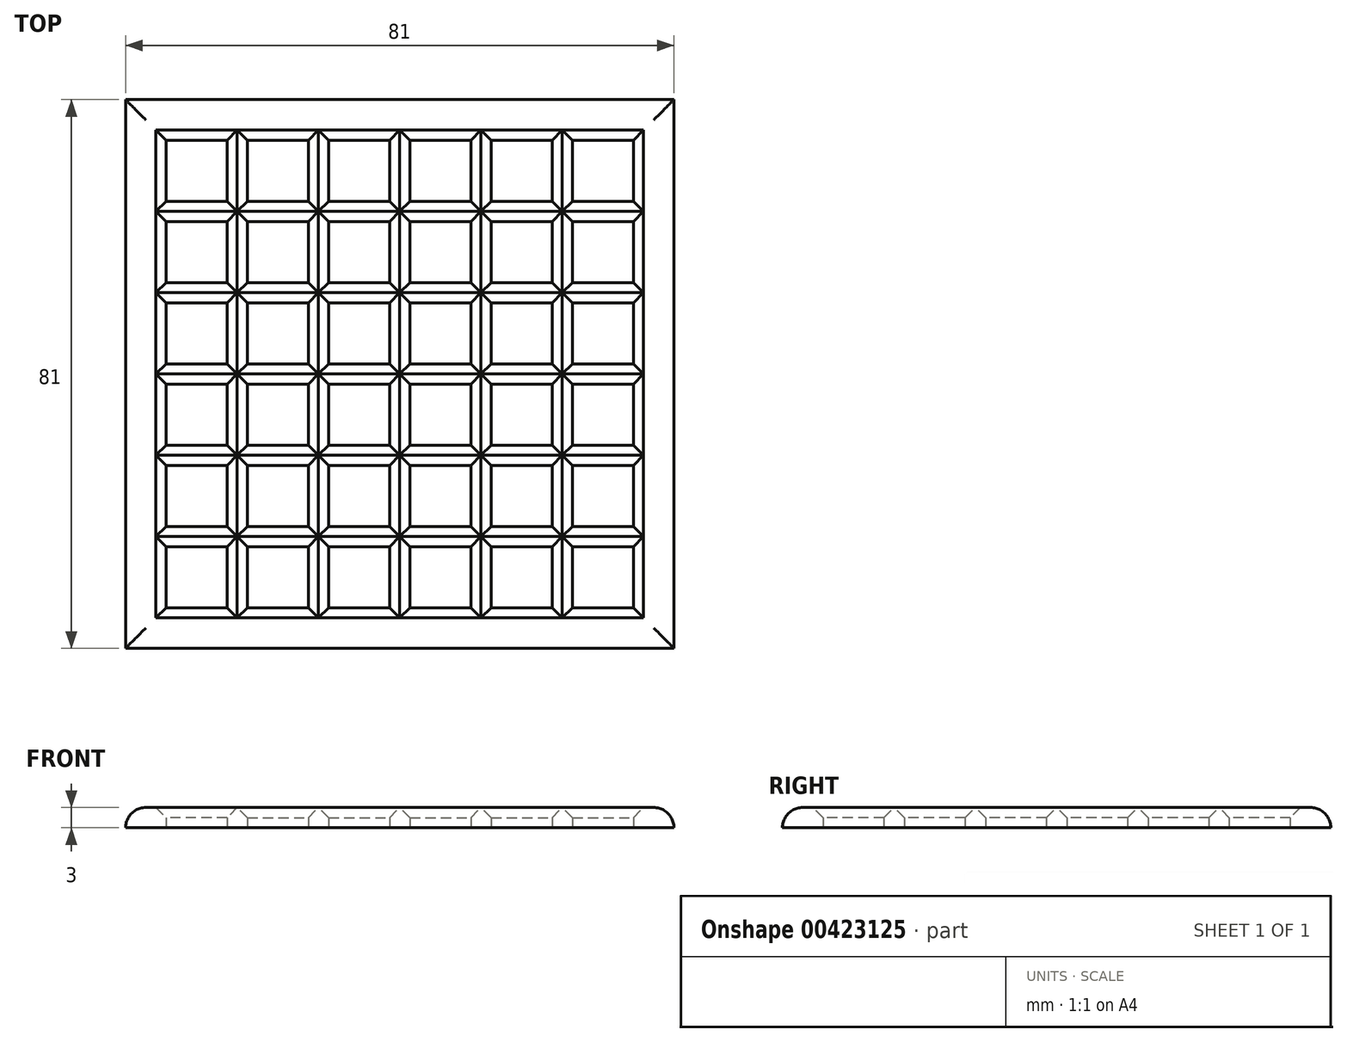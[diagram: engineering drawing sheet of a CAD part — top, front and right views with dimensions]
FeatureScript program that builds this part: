
annotation { "Feature Type Name" : "Feature", "Feature Type Description" : "" }
export const myFeature = defineFeature(function(context is Context, id is Id, definition is map)
    precondition{}
    {
        {
            var Q0;
            Q0=qCreatedBy(makeId("Top.planeOp"),FACE);
            var sketch = newSketch(context, id + "F0", { "sketchPlane" : qUnion([Q0])});
            skLineSegment(sketch, "E0.bottom", {"start": v(-69, 69) * mm, "end": v(-60, 69) * mm});
            skLineSegment(sketch, "E0.top", {"start": v(-69, 60) * mm, "end": v(-60, 60) * mm});
            skLineSegment(sketch, "E0.left", {"start": v(-69, 69) * mm, "end": v(-69, 60) * mm});
            skLineSegment(sketch, "E0.right", {"start": v(-60, 69) * mm, "end": v(-60, 60) * mm});
            skLineSegment(sketch, "E1.0.1.0", {"start": v(-69, 48) * mm, "end": v(-60, 48) * mm});
            skLineSegment(sketch, "E1.0.1.1", {"start": v(-60, 57) * mm, "end": v(-60, 48) * mm});
            skLineSegment(sketch, "E1.0.1.2", {"start": v(-69, 57) * mm, "end": v(-69, 48) * mm});
            skLineSegment(sketch, "E1.0.1.3", {"start": v(-69, 57) * mm, "end": v(-60, 57) * mm});
            skLineSegment(sketch, "E1.0.2.0", {"start": v(-69, 36) * mm, "end": v(-60, 36) * mm});
            skLineSegment(sketch, "E1.0.2.1", {"start": v(-60, 45) * mm, "end": v(-60, 36) * mm});
            skLineSegment(sketch, "E1.0.2.2", {"start": v(-69, 45) * mm, "end": v(-69, 36) * mm});
            skLineSegment(sketch, "E1.0.2.3", {"start": v(-69, 45) * mm, "end": v(-60, 45) * mm});
            skLineSegment(sketch, "E1.0.3.0", {"start": v(-69, 24) * mm, "end": v(-60, 24) * mm});
            skLineSegment(sketch, "E1.0.3.1", {"start": v(-60, 33) * mm, "end": v(-60, 24) * mm});
            skLineSegment(sketch, "E1.0.3.2", {"start": v(-69, 33) * mm, "end": v(-69, 24) * mm});
            skLineSegment(sketch, "E1.0.3.3", {"start": v(-69, 33) * mm, "end": v(-60, 33) * mm});
            skLineSegment(sketch, "E1.0.4.0", {"start": v(-69, 12) * mm, "end": v(-60, 12) * mm});
            skLineSegment(sketch, "E1.0.4.1", {"start": v(-60, 21) * mm, "end": v(-60, 12) * mm});
            skLineSegment(sketch, "E1.0.4.2", {"start": v(-69, 21) * mm, "end": v(-69, 12) * mm});
            skLineSegment(sketch, "E1.0.4.3", {"start": v(-69, 21) * mm, "end": v(-60, 21) * mm});
            skLineSegment(sketch, "E1.0.5.0", {"start": v(-69, 0) * mm, "end": v(-60, 0) * mm});
            skLineSegment(sketch, "E1.0.5.1", {"start": v(-60, 9) * mm, "end": v(-60, 0) * mm});
            skLineSegment(sketch, "E1.0.5.2", {"start": v(-69, 9) * mm, "end": v(-69, 0) * mm});
            skLineSegment(sketch, "E1.0.5.3", {"start": v(-69, 9) * mm, "end": v(-60, 9) * mm});
            skLineSegment(sketch, "E1.1.0.0", {"start": v(-57, 60) * mm, "end": v(-48, 60) * mm});
            skLineSegment(sketch, "E1.1.0.1", {"start": v(-48, 69) * mm, "end": v(-48, 60) * mm});
            skLineSegment(sketch, "E1.1.0.2", {"start": v(-57, 69) * mm, "end": v(-57, 60) * mm});
            skLineSegment(sketch, "E1.1.0.3", {"start": v(-57, 69) * mm, "end": v(-48, 69) * mm});
            skLineSegment(sketch, "E1.1.1.0", {"start": v(-57, 48) * mm, "end": v(-48, 48) * mm});
            skLineSegment(sketch, "E1.1.1.1", {"start": v(-48, 57) * mm, "end": v(-48, 48) * mm});
            skLineSegment(sketch, "E1.1.1.2", {"start": v(-57, 57) * mm, "end": v(-57, 48) * mm});
            skLineSegment(sketch, "E1.1.1.3", {"start": v(-57, 57) * mm, "end": v(-48, 57) * mm});
            skLineSegment(sketch, "E1.1.2.0", {"start": v(-57, 36) * mm, "end": v(-48, 36) * mm});
            skLineSegment(sketch, "E1.1.2.1", {"start": v(-48, 45) * mm, "end": v(-48, 36) * mm});
            skLineSegment(sketch, "E1.1.2.2", {"start": v(-57, 45) * mm, "end": v(-57, 36) * mm});
            skLineSegment(sketch, "E1.1.2.3", {"start": v(-57, 45) * mm, "end": v(-48, 45) * mm});
            skLineSegment(sketch, "E1.1.3.0", {"start": v(-57, 24) * mm, "end": v(-48, 24) * mm});
            skLineSegment(sketch, "E1.1.3.1", {"start": v(-48, 33) * mm, "end": v(-48, 24) * mm});
            skLineSegment(sketch, "E1.1.3.2", {"start": v(-57, 33) * mm, "end": v(-57, 24) * mm});
            skLineSegment(sketch, "E1.1.3.3", {"start": v(-57, 33) * mm, "end": v(-48, 33) * mm});
            skLineSegment(sketch, "E1.1.4.0", {"start": v(-57, 12) * mm, "end": v(-48, 12) * mm});
            skLineSegment(sketch, "E1.1.4.1", {"start": v(-48, 21) * mm, "end": v(-48, 12) * mm});
            skLineSegment(sketch, "E1.1.4.2", {"start": v(-57, 21) * mm, "end": v(-57, 12) * mm});
            skLineSegment(sketch, "E1.1.4.3", {"start": v(-57, 21) * mm, "end": v(-48, 21) * mm});
            skLineSegment(sketch, "E1.1.5.0", {"start": v(-57, 0) * mm, "end": v(-48, 0) * mm});
            skLineSegment(sketch, "E1.1.5.1", {"start": v(-48, 9) * mm, "end": v(-48, 0) * mm});
            skLineSegment(sketch, "E1.1.5.2", {"start": v(-57, 9) * mm, "end": v(-57, 0) * mm});
            skLineSegment(sketch, "E1.1.5.3", {"start": v(-57, 9) * mm, "end": v(-48, 9) * mm});
            skLineSegment(sketch, "E1.2.0.0", {"start": v(-45, 60) * mm, "end": v(-36, 60) * mm});
            skLineSegment(sketch, "E1.2.0.1", {"start": v(-36, 69) * mm, "end": v(-36, 60) * mm});
            skLineSegment(sketch, "E1.2.0.2", {"start": v(-45, 69) * mm, "end": v(-45, 60) * mm});
            skLineSegment(sketch, "E1.2.0.3", {"start": v(-45, 69) * mm, "end": v(-36, 69) * mm});
            skLineSegment(sketch, "E1.2.1.0", {"start": v(-45, 48) * mm, "end": v(-36, 48) * mm});
            skLineSegment(sketch, "E1.2.1.1", {"start": v(-36, 57) * mm, "end": v(-36, 48) * mm});
            skLineSegment(sketch, "E1.2.1.2", {"start": v(-45, 57) * mm, "end": v(-45, 48) * mm});
            skLineSegment(sketch, "E1.2.1.3", {"start": v(-45, 57) * mm, "end": v(-36, 57) * mm});
            skLineSegment(sketch, "E1.2.2.0", {"start": v(-45, 36) * mm, "end": v(-36, 36) * mm});
            skLineSegment(sketch, "E1.2.2.1", {"start": v(-36, 45) * mm, "end": v(-36, 36) * mm});
            skLineSegment(sketch, "E1.2.2.2", {"start": v(-45, 45) * mm, "end": v(-45, 36) * mm});
            skLineSegment(sketch, "E1.2.2.3", {"start": v(-45, 45) * mm, "end": v(-36, 45) * mm});
            skLineSegment(sketch, "E1.2.3.0", {"start": v(-45, 24) * mm, "end": v(-36, 24) * mm});
            skLineSegment(sketch, "E1.2.3.1", {"start": v(-36, 33) * mm, "end": v(-36, 24) * mm});
            skLineSegment(sketch, "E1.2.3.2", {"start": v(-45, 33) * mm, "end": v(-45, 24) * mm});
            skLineSegment(sketch, "E1.2.3.3", {"start": v(-45, 33) * mm, "end": v(-36, 33) * mm});
            skLineSegment(sketch, "E1.2.4.0", {"start": v(-45, 12) * mm, "end": v(-36, 12) * mm});
            skLineSegment(sketch, "E1.2.4.1", {"start": v(-36, 21) * mm, "end": v(-36, 12) * mm});
            skLineSegment(sketch, "E1.2.4.2", {"start": v(-45, 21) * mm, "end": v(-45, 12) * mm});
            skLineSegment(sketch, "E1.2.4.3", {"start": v(-45, 21) * mm, "end": v(-36, 21) * mm});
            skLineSegment(sketch, "E1.2.5.0", {"start": v(-45, 0) * mm, "end": v(-36, 0) * mm});
            skLineSegment(sketch, "E1.2.5.1", {"start": v(-36, 9) * mm, "end": v(-36, 0) * mm});
            skLineSegment(sketch, "E1.2.5.2", {"start": v(-45, 9) * mm, "end": v(-45, 0) * mm});
            skLineSegment(sketch, "E1.2.5.3", {"start": v(-45, 9) * mm, "end": v(-36, 9) * mm});
            skLineSegment(sketch, "E1.3.0.0", {"start": v(-33, 60) * mm, "end": v(-24, 60) * mm});
            skLineSegment(sketch, "E1.3.0.1", {"start": v(-24, 69) * mm, "end": v(-24, 60) * mm});
            skLineSegment(sketch, "E1.3.0.2", {"start": v(-33, 69) * mm, "end": v(-33, 60) * mm});
            skLineSegment(sketch, "E1.3.0.3", {"start": v(-33, 69) * mm, "end": v(-24, 69) * mm});
            skLineSegment(sketch, "E1.3.1.0", {"start": v(-33, 48) * mm, "end": v(-24, 48) * mm});
            skLineSegment(sketch, "E1.3.1.1", {"start": v(-24, 57) * mm, "end": v(-24, 48) * mm});
            skLineSegment(sketch, "E1.3.1.2", {"start": v(-33, 57) * mm, "end": v(-33, 48) * mm});
            skLineSegment(sketch, "E1.3.1.3", {"start": v(-33, 57) * mm, "end": v(-24, 57) * mm});
            skLineSegment(sketch, "E1.3.2.0", {"start": v(-33, 36) * mm, "end": v(-24, 36) * mm});
            skLineSegment(sketch, "E1.3.2.1", {"start": v(-24, 45) * mm, "end": v(-24, 36) * mm});
            skLineSegment(sketch, "E1.3.2.2", {"start": v(-33, 45) * mm, "end": v(-33, 36) * mm});
            skLineSegment(sketch, "E1.3.2.3", {"start": v(-33, 45) * mm, "end": v(-24, 45) * mm});
            skLineSegment(sketch, "E1.3.3.0", {"start": v(-33, 24) * mm, "end": v(-24, 24) * mm});
            skLineSegment(sketch, "E1.3.3.1", {"start": v(-24, 33) * mm, "end": v(-24, 24) * mm});
            skLineSegment(sketch, "E1.3.3.2", {"start": v(-33, 33) * mm, "end": v(-33, 24) * mm});
            skLineSegment(sketch, "E1.3.3.3", {"start": v(-33, 33) * mm, "end": v(-24, 33) * mm});
            skLineSegment(sketch, "E1.3.4.0", {"start": v(-33, 12) * mm, "end": v(-24, 12) * mm});
            skLineSegment(sketch, "E1.3.4.1", {"start": v(-24, 21) * mm, "end": v(-24, 12) * mm});
            skLineSegment(sketch, "E1.3.4.2", {"start": v(-33, 21) * mm, "end": v(-33, 12) * mm});
            skLineSegment(sketch, "E1.3.4.3", {"start": v(-33, 21) * mm, "end": v(-24, 21) * mm});
            skLineSegment(sketch, "E1.3.5.0", {"start": v(-33, 0) * mm, "end": v(-24, 0) * mm});
            skLineSegment(sketch, "E1.3.5.1", {"start": v(-24, 9) * mm, "end": v(-24, 0) * mm});
            skLineSegment(sketch, "E1.3.5.2", {"start": v(-33, 9) * mm, "end": v(-33, 0) * mm});
            skLineSegment(sketch, "E1.3.5.3", {"start": v(-33, 9) * mm, "end": v(-24, 9) * mm});
            skLineSegment(sketch, "E1.4.0.0", {"start": v(-21, 60) * mm, "end": v(-12, 60) * mm});
            skLineSegment(sketch, "E1.4.0.1", {"start": v(-12, 69) * mm, "end": v(-12, 60) * mm});
            skLineSegment(sketch, "E1.4.0.2", {"start": v(-21, 69) * mm, "end": v(-21, 60) * mm});
            skLineSegment(sketch, "E1.4.0.3", {"start": v(-21, 69) * mm, "end": v(-12, 69) * mm});
            skLineSegment(sketch, "E1.4.1.0", {"start": v(-21, 48) * mm, "end": v(-12, 48) * mm});
            skLineSegment(sketch, "E1.4.1.1", {"start": v(-12, 57) * mm, "end": v(-12, 48) * mm});
            skLineSegment(sketch, "E1.4.1.2", {"start": v(-21, 57) * mm, "end": v(-21, 48) * mm});
            skLineSegment(sketch, "E1.4.1.3", {"start": v(-21, 57) * mm, "end": v(-12, 57) * mm});
            skLineSegment(sketch, "E1.4.2.0", {"start": v(-21, 36) * mm, "end": v(-12, 36) * mm});
            skLineSegment(sketch, "E1.4.2.1", {"start": v(-12, 45) * mm, "end": v(-12, 36) * mm});
            skLineSegment(sketch, "E1.4.2.2", {"start": v(-21, 45) * mm, "end": v(-21, 36) * mm});
            skLineSegment(sketch, "E1.4.2.3", {"start": v(-21, 45) * mm, "end": v(-12, 45) * mm});
            skLineSegment(sketch, "E1.4.3.0", {"start": v(-21, 24) * mm, "end": v(-12, 24) * mm});
            skLineSegment(sketch, "E1.4.3.1", {"start": v(-12, 33) * mm, "end": v(-12, 24) * mm});
            skLineSegment(sketch, "E1.4.3.2", {"start": v(-21, 33) * mm, "end": v(-21, 24) * mm});
            skLineSegment(sketch, "E1.4.3.3", {"start": v(-21, 33) * mm, "end": v(-12, 33) * mm});
            skLineSegment(sketch, "E1.4.4.0", {"start": v(-21, 12) * mm, "end": v(-12, 12) * mm});
            skLineSegment(sketch, "E1.4.4.1", {"start": v(-12, 21) * mm, "end": v(-12, 12) * mm});
            skLineSegment(sketch, "E1.4.4.2", {"start": v(-21, 21) * mm, "end": v(-21, 12) * mm});
            skLineSegment(sketch, "E1.4.4.3", {"start": v(-21, 21) * mm, "end": v(-12, 21) * mm});
            skLineSegment(sketch, "E1.4.5.0", {"start": v(-21, 0) * mm, "end": v(-12, 0) * mm});
            skLineSegment(sketch, "E1.4.5.1", {"start": v(-12, 9) * mm, "end": v(-12, 0) * mm});
            skLineSegment(sketch, "E1.4.5.2", {"start": v(-21, 9) * mm, "end": v(-21, 0) * mm});
            skLineSegment(sketch, "E1.4.5.3", {"start": v(-21, 9) * mm, "end": v(-12, 9) * mm});
            skLineSegment(sketch, "E1.5.0.0", {"start": v(-9, 60) * mm, "end": v(0, 60) * mm});
            skLineSegment(sketch, "E1.5.0.1", {"start": v(0, 69) * mm, "end": v(0, 60) * mm});
            skLineSegment(sketch, "E1.5.0.2", {"start": v(-9, 69) * mm, "end": v(-9, 60) * mm});
            skLineSegment(sketch, "E1.5.0.3", {"start": v(-9, 69) * mm, "end": v(0, 69) * mm});
            skLineSegment(sketch, "E1.5.1.0", {"start": v(-9, 48) * mm, "end": v(0, 48) * mm});
            skLineSegment(sketch, "E1.5.1.1", {"start": v(0, 57) * mm, "end": v(0, 48) * mm});
            skLineSegment(sketch, "E1.5.1.2", {"start": v(-9, 57) * mm, "end": v(-9, 48) * mm});
            skLineSegment(sketch, "E1.5.1.3", {"start": v(-9, 57) * mm, "end": v(0, 57) * mm});
            skLineSegment(sketch, "E1.5.2.0", {"start": v(-9, 36) * mm, "end": v(0, 36) * mm});
            skLineSegment(sketch, "E1.5.2.1", {"start": v(0, 45) * mm, "end": v(0, 36) * mm});
            skLineSegment(sketch, "E1.5.2.2", {"start": v(-9, 45) * mm, "end": v(-9, 36) * mm});
            skLineSegment(sketch, "E1.5.2.3", {"start": v(-9, 45) * mm, "end": v(0, 45) * mm});
            skLineSegment(sketch, "E1.5.3.0", {"start": v(-9, 24) * mm, "end": v(0, 24) * mm});
            skLineSegment(sketch, "E1.5.3.1", {"start": v(0, 33) * mm, "end": v(0, 24) * mm});
            skLineSegment(sketch, "E1.5.3.2", {"start": v(-9, 33) * mm, "end": v(-9, 24) * mm});
            skLineSegment(sketch, "E1.5.3.3", {"start": v(-9, 33) * mm, "end": v(0, 33) * mm});
            skLineSegment(sketch, "E1.5.4.0", {"start": v(-9, 12) * mm, "end": v(0, 12) * mm});
            skLineSegment(sketch, "E1.5.4.1", {"start": v(0, 21) * mm, "end": v(0, 12) * mm});
            skLineSegment(sketch, "E1.5.4.2", {"start": v(-9, 21) * mm, "end": v(-9, 12) * mm});
            skLineSegment(sketch, "E1.5.4.3", {"start": v(-9, 21) * mm, "end": v(0, 21) * mm});
            skLineSegment(sketch, "E1.5.5.0", {"start": v(-9, 0) * mm, "end": v(0, 0) * mm});
            skLineSegment(sketch, "E1.5.5.1", {"start": v(0, 9) * mm, "end": v(0, 0) * mm});
            skLineSegment(sketch, "E1.5.5.2", {"start": v(-9, 9) * mm, "end": v(-9, 0) * mm});
            skLineSegment(sketch, "E1.5.5.3", {"start": v(-9, 9) * mm, "end": v(0, 9) * mm});
            skLineSegment(sketch, "E1.direction1", {"start": v(-69, 60) * mm, "end": v(-57, 60) * mm, "construction": true});
            skLineSegment(sketch, "E1.direction2", {"start": v(-69, 60) * mm, "end": v(-69, 48) * mm, "construction": true});
            skSolve(sketch);
        }
        {
            var Q0;
            Q0=qCreatedBy(makeId("Top.planeOp"),FACE);
            var sketch = newSketch(context, id + "F1", { "sketchPlane" : qUnion([Q0])});
            skLineSegment(sketch, "E2.bottom", {"start": v(-75, 75) * mm, "end": v(6, 75) * mm});
            skLineSegment(sketch, "E2.top", {"start": v(-75, -6) * mm, "end": v(6, -6) * mm});
            skLineSegment(sketch, "E2.left", {"start": v(-75, 75) * mm, "end": v(-75, -6) * mm});
            skLineSegment(sketch, "E2.right", {"start": v(6, 75) * mm, "end": v(6, -6) * mm});
            skSolve(sketch);
        }
        {
            var Q0;
            Q0=qSketchRegion(id+"F1",true);
            extrude(context, id + "F2", {"entities" : qUnion([Q0]), "depth" : 3 * mm});
        }
        {
            var Q0;
            Q0=qSketchRegion(id+"F0",true);
            extrude(context, id + "F3", {"entities" : qUnion([Q0]), "operationType" : NewBodyOperationType.REMOVE, "oppositeDirection" : true, "depth" : -5 * mm, "hasSecondDirection" : true, "secondDirectionOppositeDirection" : false, "secondDirectionDepth" : -3 * mm});
        }
        {
            var Q0;
            Q0=makeQuery(id+"F3.boolean.opBoolean","INTERSECT",EDGE,{"derivedFrom":[makeQuery(id+"F2.opExtrude","CAP_FACE",FACE,{"disambiguationData":[OSD([sQuery(id+"F1.wireOp",EDGE,"E2.bottom"),sQuery(id+"F1.wireOp",EDGE,"E2.top"),sQuery(id+"F1.wireOp",EDGE,"E2.left"),sQuery(id+"F1.wireOp",EDGE,"E2.right")])],"isStart":false}),makeQuery(id+"F3.opExtrude","SWEPT_FACE",FACE,{"disambiguationData":[OSD([sQuery(id+"F0.wireOp",EDGE,"E0.bottom")])]})]});
            var Q1;
            Q1=makeQuery(id+"F3.boolean.opBoolean","INTERSECT",EDGE,{"derivedFrom":[makeQuery(id+"F2.opExtrude","CAP_FACE",FACE,{"disambiguationData":[OSD([sQuery(id+"F1.wireOp",EDGE,"E2.bottom"),sQuery(id+"F1.wireOp",EDGE,"E2.top"),sQuery(id+"F1.wireOp",EDGE,"E2.left"),sQuery(id+"F1.wireOp",EDGE,"E2.right")])],"isStart":false}),makeQuery(id+"F3.opExtrude","SWEPT_FACE",FACE,{"disambiguationData":[OSD([sQuery(id+"F0.wireOp",EDGE,"E0.left")])]})]});
            var Q2;
            Q2=makeQuery(id+"F3.boolean.opBoolean","INTERSECT",EDGE,{"derivedFrom":[makeQuery(id+"F2.opExtrude","CAP_FACE",FACE,{"disambiguationData":[OSD([sQuery(id+"F1.wireOp",EDGE,"E2.bottom"),sQuery(id+"F1.wireOp",EDGE,"E2.top"),sQuery(id+"F1.wireOp",EDGE,"E2.left"),sQuery(id+"F1.wireOp",EDGE,"E2.right")])],"isStart":false}),makeQuery(id+"F3.opExtrude","SWEPT_FACE",FACE,{"disambiguationData":[OSD([sQuery(id+"F0.wireOp",EDGE,"E0.right")])]})]});
            var Q3;
            Q3=makeQuery(id+"F3.boolean.opBoolean","INTERSECT",EDGE,{"derivedFrom":[makeQuery(id+"F2.opExtrude","CAP_FACE",FACE,{"disambiguationData":[OSD([sQuery(id+"F1.wireOp",EDGE,"E2.bottom"),sQuery(id+"F1.wireOp",EDGE,"E2.top"),sQuery(id+"F1.wireOp",EDGE,"E2.left"),sQuery(id+"F1.wireOp",EDGE,"E2.right")])],"isStart":false}),makeQuery(id+"F3.opExtrude","SWEPT_FACE",FACE,{"disambiguationData":[OSD([sQuery(id+"F0.wireOp",EDGE,"E0.top")])]})]});
            var Q4;
            Q4=makeQuery(id+"F3.boolean.opBoolean","INTERSECT",EDGE,{"derivedFrom":[makeQuery(id+"F2.opExtrude","CAP_FACE",FACE,{"disambiguationData":[OSD([sQuery(id+"F1.wireOp",EDGE,"E2.bottom"),sQuery(id+"F1.wireOp",EDGE,"E2.top"),sQuery(id+"F1.wireOp",EDGE,"E2.left"),sQuery(id+"F1.wireOp",EDGE,"E2.right")])],"isStart":false}),makeQuery(id+"F3.opExtrude","SWEPT_FACE",FACE,{"disambiguationData":[OSD([sQuery(id+"F0.wireOp",EDGE,"E1.1.0.3")])]})]});
            var Q5;
            Q5=makeQuery(id+"F3.boolean.opBoolean","INTERSECT",EDGE,{"derivedFrom":[makeQuery(id+"F2.opExtrude","CAP_FACE",FACE,{"disambiguationData":[OSD([sQuery(id+"F1.wireOp",EDGE,"E2.bottom"),sQuery(id+"F1.wireOp",EDGE,"E2.top"),sQuery(id+"F1.wireOp",EDGE,"E2.left"),sQuery(id+"F1.wireOp",EDGE,"E2.right")])],"isStart":false}),makeQuery(id+"F3.opExtrude","SWEPT_FACE",FACE,{"disambiguationData":[OSD([sQuery(id+"F0.wireOp",EDGE,"E1.1.0.2")])]})]});
            var Q6;
            Q6=makeQuery(id+"F3.boolean.opBoolean","INTERSECT",EDGE,{"derivedFrom":[makeQuery(id+"F2.opExtrude","CAP_FACE",FACE,{"disambiguationData":[OSD([sQuery(id+"F1.wireOp",EDGE,"E2.bottom"),sQuery(id+"F1.wireOp",EDGE,"E2.top"),sQuery(id+"F1.wireOp",EDGE,"E2.left"),sQuery(id+"F1.wireOp",EDGE,"E2.right")])],"isStart":false}),makeQuery(id+"F3.opExtrude","SWEPT_FACE",FACE,{"disambiguationData":[OSD([sQuery(id+"F0.wireOp",EDGE,"E1.1.0.0")])]})]});
            var Q7;
            Q7=makeQuery(id+"F3.boolean.opBoolean","INTERSECT",EDGE,{"derivedFrom":[makeQuery(id+"F2.opExtrude","CAP_FACE",FACE,{"disambiguationData":[OSD([sQuery(id+"F1.wireOp",EDGE,"E2.bottom"),sQuery(id+"F1.wireOp",EDGE,"E2.top"),sQuery(id+"F1.wireOp",EDGE,"E2.left"),sQuery(id+"F1.wireOp",EDGE,"E2.right")])],"isStart":false}),makeQuery(id+"F3.opExtrude","SWEPT_FACE",FACE,{"disambiguationData":[OSD([sQuery(id+"F0.wireOp",EDGE,"E1.1.0.1")])]})]});
            var Q8;
            Q8=makeQuery(id+"F3.boolean.opBoolean","INTERSECT",EDGE,{"derivedFrom":[makeQuery(id+"F2.opExtrude","CAP_FACE",FACE,{"disambiguationData":[OSD([sQuery(id+"F1.wireOp",EDGE,"E2.bottom"),sQuery(id+"F1.wireOp",EDGE,"E2.top"),sQuery(id+"F1.wireOp",EDGE,"E2.left"),sQuery(id+"F1.wireOp",EDGE,"E2.right")])],"isStart":false}),makeQuery(id+"F3.opExtrude","SWEPT_FACE",FACE,{"disambiguationData":[OSD([sQuery(id+"F0.wireOp",EDGE,"E1.2.0.2")])]})]});
            var Q9;
            Q9=makeQuery(id+"F3.boolean.opBoolean","INTERSECT",EDGE,{"derivedFrom":[makeQuery(id+"F2.opExtrude","CAP_FACE",FACE,{"disambiguationData":[OSD([sQuery(id+"F1.wireOp",EDGE,"E2.bottom"),sQuery(id+"F1.wireOp",EDGE,"E2.top"),sQuery(id+"F1.wireOp",EDGE,"E2.left"),sQuery(id+"F1.wireOp",EDGE,"E2.right")])],"isStart":false}),makeQuery(id+"F3.opExtrude","SWEPT_FACE",FACE,{"disambiguationData":[OSD([sQuery(id+"F0.wireOp",EDGE,"E1.2.0.1")])]})]});
            var Q10;
            Q10=makeQuery(id+"F3.boolean.opBoolean","INTERSECT",EDGE,{"derivedFrom":[makeQuery(id+"F2.opExtrude","CAP_FACE",FACE,{"disambiguationData":[OSD([sQuery(id+"F1.wireOp",EDGE,"E2.bottom"),sQuery(id+"F1.wireOp",EDGE,"E2.top"),sQuery(id+"F1.wireOp",EDGE,"E2.left"),sQuery(id+"F1.wireOp",EDGE,"E2.right")])],"isStart":false}),makeQuery(id+"F3.opExtrude","SWEPT_FACE",FACE,{"disambiguationData":[OSD([sQuery(id+"F0.wireOp",EDGE,"E1.3.0.2")])]})]});
            var Q11;
            Q11=makeQuery(id+"F3.boolean.opBoolean","INTERSECT",EDGE,{"derivedFrom":[makeQuery(id+"F2.opExtrude","CAP_FACE",FACE,{"disambiguationData":[OSD([sQuery(id+"F1.wireOp",EDGE,"E2.bottom"),sQuery(id+"F1.wireOp",EDGE,"E2.top"),sQuery(id+"F1.wireOp",EDGE,"E2.left"),sQuery(id+"F1.wireOp",EDGE,"E2.right")])],"isStart":false}),makeQuery(id+"F3.opExtrude","SWEPT_FACE",FACE,{"disambiguationData":[OSD([sQuery(id+"F0.wireOp",EDGE,"E1.3.0.1")])]})]});
            var Q12;
            Q12=makeQuery(id+"F3.boolean.opBoolean","INTERSECT",EDGE,{"derivedFrom":[makeQuery(id+"F2.opExtrude","CAP_FACE",FACE,{"disambiguationData":[OSD([sQuery(id+"F1.wireOp",EDGE,"E2.bottom"),sQuery(id+"F1.wireOp",EDGE,"E2.top"),sQuery(id+"F1.wireOp",EDGE,"E2.left"),sQuery(id+"F1.wireOp",EDGE,"E2.right")])],"isStart":false}),makeQuery(id+"F3.opExtrude","SWEPT_FACE",FACE,{"disambiguationData":[OSD([sQuery(id+"F0.wireOp",EDGE,"E1.4.0.2")])]})]});
            var Q13;
            Q13=makeQuery(id+"F3.boolean.opBoolean","INTERSECT",EDGE,{"derivedFrom":[makeQuery(id+"F2.opExtrude","CAP_FACE",FACE,{"disambiguationData":[OSD([sQuery(id+"F1.wireOp",EDGE,"E2.bottom"),sQuery(id+"F1.wireOp",EDGE,"E2.top"),sQuery(id+"F1.wireOp",EDGE,"E2.left"),sQuery(id+"F1.wireOp",EDGE,"E2.right")])],"isStart":false}),makeQuery(id+"F3.opExtrude","SWEPT_FACE",FACE,{"disambiguationData":[OSD([sQuery(id+"F0.wireOp",EDGE,"E1.4.0.1")])]})]});
            var Q14;
            Q14=makeQuery(id+"F3.boolean.opBoolean","INTERSECT",EDGE,{"derivedFrom":[makeQuery(id+"F2.opExtrude","CAP_FACE",FACE,{"disambiguationData":[OSD([sQuery(id+"F1.wireOp",EDGE,"E2.bottom"),sQuery(id+"F1.wireOp",EDGE,"E2.top"),sQuery(id+"F1.wireOp",EDGE,"E2.left"),sQuery(id+"F1.wireOp",EDGE,"E2.right")])],"isStart":false}),makeQuery(id+"F3.opExtrude","SWEPT_FACE",FACE,{"disambiguationData":[OSD([sQuery(id+"F0.wireOp",EDGE,"E1.5.0.2")])]})]});
            var Q15;
            Q15=makeQuery(id+"F3.boolean.opBoolean","INTERSECT",EDGE,{"derivedFrom":[makeQuery(id+"F2.opExtrude","CAP_FACE",FACE,{"disambiguationData":[OSD([sQuery(id+"F1.wireOp",EDGE,"E2.bottom"),sQuery(id+"F1.wireOp",EDGE,"E2.top"),sQuery(id+"F1.wireOp",EDGE,"E2.left"),sQuery(id+"F1.wireOp",EDGE,"E2.right")])],"isStart":false}),makeQuery(id+"F3.opExtrude","SWEPT_FACE",FACE,{"disambiguationData":[OSD([sQuery(id+"F0.wireOp",EDGE,"E1.5.0.1")])]})]});
            var Q16;
            Q16=makeQuery(id+"F3.boolean.opBoolean","INTERSECT",EDGE,{"derivedFrom":[makeQuery(id+"F2.opExtrude","CAP_FACE",FACE,{"disambiguationData":[OSD([sQuery(id+"F1.wireOp",EDGE,"E2.bottom"),sQuery(id+"F1.wireOp",EDGE,"E2.top"),sQuery(id+"F1.wireOp",EDGE,"E2.left"),sQuery(id+"F1.wireOp",EDGE,"E2.right")])],"isStart":false}),makeQuery(id+"F3.opExtrude","SWEPT_FACE",FACE,{"disambiguationData":[OSD([sQuery(id+"F0.wireOp",EDGE,"E1.0.1.2")])]})]});
            var Q17;
            Q17=makeQuery(id+"F3.boolean.opBoolean","INTERSECT",EDGE,{"derivedFrom":[makeQuery(id+"F2.opExtrude","CAP_FACE",FACE,{"disambiguationData":[OSD([sQuery(id+"F1.wireOp",EDGE,"E2.bottom"),sQuery(id+"F1.wireOp",EDGE,"E2.top"),sQuery(id+"F1.wireOp",EDGE,"E2.left"),sQuery(id+"F1.wireOp",EDGE,"E2.right")])],"isStart":false}),makeQuery(id+"F3.opExtrude","SWEPT_FACE",FACE,{"disambiguationData":[OSD([sQuery(id+"F0.wireOp",EDGE,"E1.0.1.1")])]})]});
            var Q18;
            Q18=makeQuery(id+"F3.boolean.opBoolean","INTERSECT",EDGE,{"derivedFrom":[makeQuery(id+"F2.opExtrude","CAP_FACE",FACE,{"disambiguationData":[OSD([sQuery(id+"F1.wireOp",EDGE,"E2.bottom"),sQuery(id+"F1.wireOp",EDGE,"E2.top"),sQuery(id+"F1.wireOp",EDGE,"E2.left"),sQuery(id+"F1.wireOp",EDGE,"E2.right")])],"isStart":false}),makeQuery(id+"F3.opExtrude","SWEPT_FACE",FACE,{"disambiguationData":[OSD([sQuery(id+"F0.wireOp",EDGE,"E1.1.1.2")])]})]});
            var Q19;
            Q19=makeQuery(id+"F3.boolean.opBoolean","INTERSECT",EDGE,{"derivedFrom":[makeQuery(id+"F2.opExtrude","CAP_FACE",FACE,{"disambiguationData":[OSD([sQuery(id+"F1.wireOp",EDGE,"E2.bottom"),sQuery(id+"F1.wireOp",EDGE,"E2.top"),sQuery(id+"F1.wireOp",EDGE,"E2.left"),sQuery(id+"F1.wireOp",EDGE,"E2.right")])],"isStart":false}),makeQuery(id+"F3.opExtrude","SWEPT_FACE",FACE,{"disambiguationData":[OSD([sQuery(id+"F0.wireOp",EDGE,"E1.1.1.1")])]})]});
            var Q20;
            Q20=makeQuery(id+"F3.boolean.opBoolean","INTERSECT",EDGE,{"derivedFrom":[makeQuery(id+"F2.opExtrude","CAP_FACE",FACE,{"disambiguationData":[OSD([sQuery(id+"F1.wireOp",EDGE,"E2.bottom"),sQuery(id+"F1.wireOp",EDGE,"E2.top"),sQuery(id+"F1.wireOp",EDGE,"E2.left"),sQuery(id+"F1.wireOp",EDGE,"E2.right")])],"isStart":false}),makeQuery(id+"F3.opExtrude","SWEPT_FACE",FACE,{"disambiguationData":[OSD([sQuery(id+"F0.wireOp",EDGE,"E1.2.1.2")])]})]});
            var Q21;
            Q21=makeQuery(id+"F3.boolean.opBoolean","INTERSECT",EDGE,{"derivedFrom":[makeQuery(id+"F2.opExtrude","CAP_FACE",FACE,{"disambiguationData":[OSD([sQuery(id+"F1.wireOp",EDGE,"E2.bottom"),sQuery(id+"F1.wireOp",EDGE,"E2.top"),sQuery(id+"F1.wireOp",EDGE,"E2.left"),sQuery(id+"F1.wireOp",EDGE,"E2.right")])],"isStart":false}),makeQuery(id+"F3.opExtrude","SWEPT_FACE",FACE,{"disambiguationData":[OSD([sQuery(id+"F0.wireOp",EDGE,"E1.2.1.1")])]})]});
            var Q22;
            Q22=makeQuery(id+"F3.boolean.opBoolean","INTERSECT",EDGE,{"derivedFrom":[makeQuery(id+"F2.opExtrude","CAP_FACE",FACE,{"disambiguationData":[OSD([sQuery(id+"F1.wireOp",EDGE,"E2.bottom"),sQuery(id+"F1.wireOp",EDGE,"E2.top"),sQuery(id+"F1.wireOp",EDGE,"E2.left"),sQuery(id+"F1.wireOp",EDGE,"E2.right")])],"isStart":false}),makeQuery(id+"F3.opExtrude","SWEPT_FACE",FACE,{"disambiguationData":[OSD([sQuery(id+"F0.wireOp",EDGE,"E1.3.1.2")])]})]});
            var Q23;
            Q23=makeQuery(id+"F3.boolean.opBoolean","INTERSECT",EDGE,{"derivedFrom":[makeQuery(id+"F2.opExtrude","CAP_FACE",FACE,{"disambiguationData":[OSD([sQuery(id+"F1.wireOp",EDGE,"E2.bottom"),sQuery(id+"F1.wireOp",EDGE,"E2.top"),sQuery(id+"F1.wireOp",EDGE,"E2.left"),sQuery(id+"F1.wireOp",EDGE,"E2.right")])],"isStart":false}),makeQuery(id+"F3.opExtrude","SWEPT_FACE",FACE,{"disambiguationData":[OSD([sQuery(id+"F0.wireOp",EDGE,"E1.3.1.1")])]})]});
            var Q24;
            Q24=makeQuery(id+"F3.boolean.opBoolean","INTERSECT",EDGE,{"derivedFrom":[makeQuery(id+"F2.opExtrude","CAP_FACE",FACE,{"disambiguationData":[OSD([sQuery(id+"F1.wireOp",EDGE,"E2.bottom"),sQuery(id+"F1.wireOp",EDGE,"E2.top"),sQuery(id+"F1.wireOp",EDGE,"E2.left"),sQuery(id+"F1.wireOp",EDGE,"E2.right")])],"isStart":false}),makeQuery(id+"F3.opExtrude","SWEPT_FACE",FACE,{"disambiguationData":[OSD([sQuery(id+"F0.wireOp",EDGE,"E1.4.1.2")])]})]});
            var Q25;
            Q25=makeQuery(id+"F3.boolean.opBoolean","INTERSECT",EDGE,{"derivedFrom":[makeQuery(id+"F2.opExtrude","CAP_FACE",FACE,{"disambiguationData":[OSD([sQuery(id+"F1.wireOp",EDGE,"E2.bottom"),sQuery(id+"F1.wireOp",EDGE,"E2.top"),sQuery(id+"F1.wireOp",EDGE,"E2.left"),sQuery(id+"F1.wireOp",EDGE,"E2.right")])],"isStart":false}),makeQuery(id+"F3.opExtrude","SWEPT_FACE",FACE,{"disambiguationData":[OSD([sQuery(id+"F0.wireOp",EDGE,"E1.4.1.1")])]})]});
            var Q26;
            Q26=makeQuery(id+"F3.boolean.opBoolean","INTERSECT",EDGE,{"derivedFrom":[makeQuery(id+"F2.opExtrude","CAP_FACE",FACE,{"disambiguationData":[OSD([sQuery(id+"F1.wireOp",EDGE,"E2.bottom"),sQuery(id+"F1.wireOp",EDGE,"E2.top"),sQuery(id+"F1.wireOp",EDGE,"E2.left"),sQuery(id+"F1.wireOp",EDGE,"E2.right")])],"isStart":false}),makeQuery(id+"F3.opExtrude","SWEPT_FACE",FACE,{"disambiguationData":[OSD([sQuery(id+"F0.wireOp",EDGE,"E1.5.1.2")])]})]});
            var Q27;
            Q27=makeQuery(id+"F3.boolean.opBoolean","INTERSECT",EDGE,{"derivedFrom":[makeQuery(id+"F2.opExtrude","CAP_FACE",FACE,{"disambiguationData":[OSD([sQuery(id+"F1.wireOp",EDGE,"E2.bottom"),sQuery(id+"F1.wireOp",EDGE,"E2.top"),sQuery(id+"F1.wireOp",EDGE,"E2.left"),sQuery(id+"F1.wireOp",EDGE,"E2.right")])],"isStart":false}),makeQuery(id+"F3.opExtrude","SWEPT_FACE",FACE,{"disambiguationData":[OSD([sQuery(id+"F0.wireOp",EDGE,"E1.5.1.1")])]})]});
            var Q28;
            Q28=makeQuery(id+"F3.boolean.opBoolean","INTERSECT",EDGE,{"derivedFrom":[makeQuery(id+"F2.opExtrude","CAP_FACE",FACE,{"disambiguationData":[OSD([sQuery(id+"F1.wireOp",EDGE,"E2.bottom"),sQuery(id+"F1.wireOp",EDGE,"E2.top"),sQuery(id+"F1.wireOp",EDGE,"E2.left"),sQuery(id+"F1.wireOp",EDGE,"E2.right")])],"isStart":false}),makeQuery(id+"F3.opExtrude","SWEPT_FACE",FACE,{"disambiguationData":[OSD([sQuery(id+"F0.wireOp",EDGE,"E1.0.2.2")])]})]});
            var Q29;
            Q29=makeQuery(id+"F3.boolean.opBoolean","INTERSECT",EDGE,{"derivedFrom":[makeQuery(id+"F2.opExtrude","CAP_FACE",FACE,{"disambiguationData":[OSD([sQuery(id+"F1.wireOp",EDGE,"E2.bottom"),sQuery(id+"F1.wireOp",EDGE,"E2.top"),sQuery(id+"F1.wireOp",EDGE,"E2.left"),sQuery(id+"F1.wireOp",EDGE,"E2.right")])],"isStart":false}),makeQuery(id+"F3.opExtrude","SWEPT_FACE",FACE,{"disambiguationData":[OSD([sQuery(id+"F0.wireOp",EDGE,"E1.0.2.1")])]})]});
            var Q30;
            Q30=makeQuery(id+"F3.boolean.opBoolean","INTERSECT",EDGE,{"derivedFrom":[makeQuery(id+"F2.opExtrude","CAP_FACE",FACE,{"disambiguationData":[OSD([sQuery(id+"F1.wireOp",EDGE,"E2.bottom"),sQuery(id+"F1.wireOp",EDGE,"E2.top"),sQuery(id+"F1.wireOp",EDGE,"E2.left"),sQuery(id+"F1.wireOp",EDGE,"E2.right")])],"isStart":false}),makeQuery(id+"F3.opExtrude","SWEPT_FACE",FACE,{"disambiguationData":[OSD([sQuery(id+"F0.wireOp",EDGE,"E1.1.2.2")])]})]});
            var Q31;
            Q31=makeQuery(id+"F3.boolean.opBoolean","INTERSECT",EDGE,{"derivedFrom":[makeQuery(id+"F2.opExtrude","CAP_FACE",FACE,{"disambiguationData":[OSD([sQuery(id+"F1.wireOp",EDGE,"E2.bottom"),sQuery(id+"F1.wireOp",EDGE,"E2.top"),sQuery(id+"F1.wireOp",EDGE,"E2.left"),sQuery(id+"F1.wireOp",EDGE,"E2.right")])],"isStart":false}),makeQuery(id+"F3.opExtrude","SWEPT_FACE",FACE,{"disambiguationData":[OSD([sQuery(id+"F0.wireOp",EDGE,"E1.1.2.1")])]})]});
            var Q32;
            Q32=makeQuery(id+"F3.boolean.opBoolean","INTERSECT",EDGE,{"derivedFrom":[makeQuery(id+"F2.opExtrude","CAP_FACE",FACE,{"disambiguationData":[OSD([sQuery(id+"F1.wireOp",EDGE,"E2.bottom"),sQuery(id+"F1.wireOp",EDGE,"E2.top"),sQuery(id+"F1.wireOp",EDGE,"E2.left"),sQuery(id+"F1.wireOp",EDGE,"E2.right")])],"isStart":false}),makeQuery(id+"F3.opExtrude","SWEPT_FACE",FACE,{"disambiguationData":[OSD([sQuery(id+"F0.wireOp",EDGE,"E1.2.2.2")])]})]});
            var Q33;
            Q33=makeQuery(id+"F3.boolean.opBoolean","INTERSECT",EDGE,{"derivedFrom":[makeQuery(id+"F2.opExtrude","CAP_FACE",FACE,{"disambiguationData":[OSD([sQuery(id+"F1.wireOp",EDGE,"E2.bottom"),sQuery(id+"F1.wireOp",EDGE,"E2.top"),sQuery(id+"F1.wireOp",EDGE,"E2.left"),sQuery(id+"F1.wireOp",EDGE,"E2.right")])],"isStart":false}),makeQuery(id+"F3.opExtrude","SWEPT_FACE",FACE,{"disambiguationData":[OSD([sQuery(id+"F0.wireOp",EDGE,"E1.2.2.1")])]})]});
            var Q34;
            Q34=makeQuery(id+"F3.boolean.opBoolean","INTERSECT",EDGE,{"derivedFrom":[makeQuery(id+"F2.opExtrude","CAP_FACE",FACE,{"disambiguationData":[OSD([sQuery(id+"F1.wireOp",EDGE,"E2.bottom"),sQuery(id+"F1.wireOp",EDGE,"E2.top"),sQuery(id+"F1.wireOp",EDGE,"E2.left"),sQuery(id+"F1.wireOp",EDGE,"E2.right")])],"isStart":false}),makeQuery(id+"F3.opExtrude","SWEPT_FACE",FACE,{"disambiguationData":[OSD([sQuery(id+"F0.wireOp",EDGE,"E1.3.2.2")])]})]});
            var Q35;
            Q35=makeQuery(id+"F3.boolean.opBoolean","INTERSECT",EDGE,{"derivedFrom":[makeQuery(id+"F2.opExtrude","CAP_FACE",FACE,{"disambiguationData":[OSD([sQuery(id+"F1.wireOp",EDGE,"E2.bottom"),sQuery(id+"F1.wireOp",EDGE,"E2.top"),sQuery(id+"F1.wireOp",EDGE,"E2.left"),sQuery(id+"F1.wireOp",EDGE,"E2.right")])],"isStart":false}),makeQuery(id+"F3.opExtrude","SWEPT_FACE",FACE,{"disambiguationData":[OSD([sQuery(id+"F0.wireOp",EDGE,"E1.3.2.1")])]})]});
            var Q36;
            Q36=makeQuery(id+"F3.boolean.opBoolean","INTERSECT",EDGE,{"derivedFrom":[makeQuery(id+"F2.opExtrude","CAP_FACE",FACE,{"disambiguationData":[OSD([sQuery(id+"F1.wireOp",EDGE,"E2.bottom"),sQuery(id+"F1.wireOp",EDGE,"E2.top"),sQuery(id+"F1.wireOp",EDGE,"E2.left"),sQuery(id+"F1.wireOp",EDGE,"E2.right")])],"isStart":false}),makeQuery(id+"F3.opExtrude","SWEPT_FACE",FACE,{"disambiguationData":[OSD([sQuery(id+"F0.wireOp",EDGE,"E1.4.2.2")])]})]});
            var Q37;
            Q37=makeQuery(id+"F3.boolean.opBoolean","INTERSECT",EDGE,{"derivedFrom":[makeQuery(id+"F2.opExtrude","CAP_FACE",FACE,{"disambiguationData":[OSD([sQuery(id+"F1.wireOp",EDGE,"E2.bottom"),sQuery(id+"F1.wireOp",EDGE,"E2.top"),sQuery(id+"F1.wireOp",EDGE,"E2.left"),sQuery(id+"F1.wireOp",EDGE,"E2.right")])],"isStart":false}),makeQuery(id+"F3.opExtrude","SWEPT_FACE",FACE,{"disambiguationData":[OSD([sQuery(id+"F0.wireOp",EDGE,"E1.4.2.1")])]})]});
            var Q38;
            Q38=makeQuery(id+"F3.boolean.opBoolean","INTERSECT",EDGE,{"derivedFrom":[makeQuery(id+"F2.opExtrude","CAP_FACE",FACE,{"disambiguationData":[OSD([sQuery(id+"F1.wireOp",EDGE,"E2.bottom"),sQuery(id+"F1.wireOp",EDGE,"E2.top"),sQuery(id+"F1.wireOp",EDGE,"E2.left"),sQuery(id+"F1.wireOp",EDGE,"E2.right")])],"isStart":false}),makeQuery(id+"F3.opExtrude","SWEPT_FACE",FACE,{"disambiguationData":[OSD([sQuery(id+"F0.wireOp",EDGE,"E1.5.2.2")])]})]});
            var Q39;
            Q39=makeQuery(id+"F3.boolean.opBoolean","INTERSECT",EDGE,{"derivedFrom":[makeQuery(id+"F2.opExtrude","CAP_FACE",FACE,{"disambiguationData":[OSD([sQuery(id+"F1.wireOp",EDGE,"E2.bottom"),sQuery(id+"F1.wireOp",EDGE,"E2.top"),sQuery(id+"F1.wireOp",EDGE,"E2.left"),sQuery(id+"F1.wireOp",EDGE,"E2.right")])],"isStart":false}),makeQuery(id+"F3.opExtrude","SWEPT_FACE",FACE,{"disambiguationData":[OSD([sQuery(id+"F0.wireOp",EDGE,"E1.5.2.1")])]})]});
            var Q40;
            Q40=makeQuery(id+"F3.boolean.opBoolean","INTERSECT",EDGE,{"derivedFrom":[makeQuery(id+"F2.opExtrude","CAP_FACE",FACE,{"disambiguationData":[OSD([sQuery(id+"F1.wireOp",EDGE,"E2.bottom"),sQuery(id+"F1.wireOp",EDGE,"E2.top"),sQuery(id+"F1.wireOp",EDGE,"E2.left"),sQuery(id+"F1.wireOp",EDGE,"E2.right")])],"isStart":false}),makeQuery(id+"F3.opExtrude","SWEPT_FACE",FACE,{"disambiguationData":[OSD([sQuery(id+"F0.wireOp",EDGE,"E1.0.3.2")])]})]});
            var Q41;
            Q41=makeQuery(id+"F3.boolean.opBoolean","INTERSECT",EDGE,{"derivedFrom":[makeQuery(id+"F2.opExtrude","CAP_FACE",FACE,{"disambiguationData":[OSD([sQuery(id+"F1.wireOp",EDGE,"E2.bottom"),sQuery(id+"F1.wireOp",EDGE,"E2.top"),sQuery(id+"F1.wireOp",EDGE,"E2.left"),sQuery(id+"F1.wireOp",EDGE,"E2.right")])],"isStart":false}),makeQuery(id+"F3.opExtrude","SWEPT_FACE",FACE,{"disambiguationData":[OSD([sQuery(id+"F0.wireOp",EDGE,"E1.0.3.1")])]})]});
            var Q42;
            Q42=makeQuery(id+"F3.boolean.opBoolean","INTERSECT",EDGE,{"derivedFrom":[makeQuery(id+"F2.opExtrude","CAP_FACE",FACE,{"disambiguationData":[OSD([sQuery(id+"F1.wireOp",EDGE,"E2.bottom"),sQuery(id+"F1.wireOp",EDGE,"E2.top"),sQuery(id+"F1.wireOp",EDGE,"E2.left"),sQuery(id+"F1.wireOp",EDGE,"E2.right")])],"isStart":false}),makeQuery(id+"F3.opExtrude","SWEPT_FACE",FACE,{"disambiguationData":[OSD([sQuery(id+"F0.wireOp",EDGE,"E1.1.3.2")])]})]});
            var Q43;
            Q43=makeQuery(id+"F3.boolean.opBoolean","INTERSECT",EDGE,{"derivedFrom":[makeQuery(id+"F2.opExtrude","CAP_FACE",FACE,{"disambiguationData":[OSD([sQuery(id+"F1.wireOp",EDGE,"E2.bottom"),sQuery(id+"F1.wireOp",EDGE,"E2.top"),sQuery(id+"F1.wireOp",EDGE,"E2.left"),sQuery(id+"F1.wireOp",EDGE,"E2.right")])],"isStart":false}),makeQuery(id+"F3.opExtrude","SWEPT_FACE",FACE,{"disambiguationData":[OSD([sQuery(id+"F0.wireOp",EDGE,"E1.1.3.1")])]})]});
            var Q44;
            Q44=makeQuery(id+"F3.boolean.opBoolean","INTERSECT",EDGE,{"derivedFrom":[makeQuery(id+"F2.opExtrude","CAP_FACE",FACE,{"disambiguationData":[OSD([sQuery(id+"F1.wireOp",EDGE,"E2.bottom"),sQuery(id+"F1.wireOp",EDGE,"E2.top"),sQuery(id+"F1.wireOp",EDGE,"E2.left"),sQuery(id+"F1.wireOp",EDGE,"E2.right")])],"isStart":false}),makeQuery(id+"F3.opExtrude","SWEPT_FACE",FACE,{"disambiguationData":[OSD([sQuery(id+"F0.wireOp",EDGE,"E1.2.3.2")])]})]});
            var Q45;
            Q45=makeQuery(id+"F3.boolean.opBoolean","INTERSECT",EDGE,{"derivedFrom":[makeQuery(id+"F2.opExtrude","CAP_FACE",FACE,{"disambiguationData":[OSD([sQuery(id+"F1.wireOp",EDGE,"E2.bottom"),sQuery(id+"F1.wireOp",EDGE,"E2.top"),sQuery(id+"F1.wireOp",EDGE,"E2.left"),sQuery(id+"F1.wireOp",EDGE,"E2.right")])],"isStart":false}),makeQuery(id+"F3.opExtrude","SWEPT_FACE",FACE,{"disambiguationData":[OSD([sQuery(id+"F0.wireOp",EDGE,"E1.2.3.1")])]})]});
            var Q46;
            Q46=makeQuery(id+"F3.boolean.opBoolean","INTERSECT",EDGE,{"derivedFrom":[makeQuery(id+"F2.opExtrude","CAP_FACE",FACE,{"disambiguationData":[OSD([sQuery(id+"F1.wireOp",EDGE,"E2.bottom"),sQuery(id+"F1.wireOp",EDGE,"E2.top"),sQuery(id+"F1.wireOp",EDGE,"E2.left"),sQuery(id+"F1.wireOp",EDGE,"E2.right")])],"isStart":false}),makeQuery(id+"F3.opExtrude","SWEPT_FACE",FACE,{"disambiguationData":[OSD([sQuery(id+"F0.wireOp",EDGE,"E1.3.3.2")])]})]});
            var Q47;
            Q47=makeQuery(id+"F3.boolean.opBoolean","INTERSECT",EDGE,{"derivedFrom":[makeQuery(id+"F2.opExtrude","CAP_FACE",FACE,{"disambiguationData":[OSD([sQuery(id+"F1.wireOp",EDGE,"E2.bottom"),sQuery(id+"F1.wireOp",EDGE,"E2.top"),sQuery(id+"F1.wireOp",EDGE,"E2.left"),sQuery(id+"F1.wireOp",EDGE,"E2.right")])],"isStart":false}),makeQuery(id+"F3.opExtrude","SWEPT_FACE",FACE,{"disambiguationData":[OSD([sQuery(id+"F0.wireOp",EDGE,"E1.3.3.1")])]})]});
            var Q48;
            Q48=makeQuery(id+"F3.boolean.opBoolean","INTERSECT",EDGE,{"derivedFrom":[makeQuery(id+"F2.opExtrude","CAP_FACE",FACE,{"disambiguationData":[OSD([sQuery(id+"F1.wireOp",EDGE,"E2.bottom"),sQuery(id+"F1.wireOp",EDGE,"E2.top"),sQuery(id+"F1.wireOp",EDGE,"E2.left"),sQuery(id+"F1.wireOp",EDGE,"E2.right")])],"isStart":false}),makeQuery(id+"F3.opExtrude","SWEPT_FACE",FACE,{"disambiguationData":[OSD([sQuery(id+"F0.wireOp",EDGE,"E1.4.3.2")])]})]});
            var Q49;
            Q49=makeQuery(id+"F3.boolean.opBoolean","INTERSECT",EDGE,{"derivedFrom":[makeQuery(id+"F2.opExtrude","CAP_FACE",FACE,{"disambiguationData":[OSD([sQuery(id+"F1.wireOp",EDGE,"E2.bottom"),sQuery(id+"F1.wireOp",EDGE,"E2.top"),sQuery(id+"F1.wireOp",EDGE,"E2.left"),sQuery(id+"F1.wireOp",EDGE,"E2.right")])],"isStart":false}),makeQuery(id+"F3.opExtrude","SWEPT_FACE",FACE,{"disambiguationData":[OSD([sQuery(id+"F0.wireOp",EDGE,"E1.4.3.1")])]})]});
            var Q50;
            Q50=makeQuery(id+"F3.boolean.opBoolean","INTERSECT",EDGE,{"derivedFrom":[makeQuery(id+"F2.opExtrude","CAP_FACE",FACE,{"disambiguationData":[OSD([sQuery(id+"F1.wireOp",EDGE,"E2.bottom"),sQuery(id+"F1.wireOp",EDGE,"E2.top"),sQuery(id+"F1.wireOp",EDGE,"E2.left"),sQuery(id+"F1.wireOp",EDGE,"E2.right")])],"isStart":false}),makeQuery(id+"F3.opExtrude","SWEPT_FACE",FACE,{"disambiguationData":[OSD([sQuery(id+"F0.wireOp",EDGE,"E1.5.3.2")])]})]});
            var Q51;
            Q51=makeQuery(id+"F3.boolean.opBoolean","INTERSECT",EDGE,{"derivedFrom":[makeQuery(id+"F2.opExtrude","CAP_FACE",FACE,{"disambiguationData":[OSD([sQuery(id+"F1.wireOp",EDGE,"E2.bottom"),sQuery(id+"F1.wireOp",EDGE,"E2.top"),sQuery(id+"F1.wireOp",EDGE,"E2.left"),sQuery(id+"F1.wireOp",EDGE,"E2.right")])],"isStart":false}),makeQuery(id+"F3.opExtrude","SWEPT_FACE",FACE,{"disambiguationData":[OSD([sQuery(id+"F0.wireOp",EDGE,"E1.5.3.1")])]})]});
            var Q52;
            Q52=makeQuery(id+"F3.boolean.opBoolean","INTERSECT",EDGE,{"derivedFrom":[makeQuery(id+"F2.opExtrude","CAP_FACE",FACE,{"disambiguationData":[OSD([sQuery(id+"F1.wireOp",EDGE,"E2.bottom"),sQuery(id+"F1.wireOp",EDGE,"E2.top"),sQuery(id+"F1.wireOp",EDGE,"E2.left"),sQuery(id+"F1.wireOp",EDGE,"E2.right")])],"isStart":false}),makeQuery(id+"F3.opExtrude","SWEPT_FACE",FACE,{"disambiguationData":[OSD([sQuery(id+"F0.wireOp",EDGE,"E1.5.4.1")])]})]});
            var Q53;
            Q53=makeQuery(id+"F3.boolean.opBoolean","INTERSECT",EDGE,{"derivedFrom":[makeQuery(id+"F2.opExtrude","CAP_FACE",FACE,{"disambiguationData":[OSD([sQuery(id+"F1.wireOp",EDGE,"E2.bottom"),sQuery(id+"F1.wireOp",EDGE,"E2.top"),sQuery(id+"F1.wireOp",EDGE,"E2.left"),sQuery(id+"F1.wireOp",EDGE,"E2.right")])],"isStart":false}),makeQuery(id+"F3.opExtrude","SWEPT_FACE",FACE,{"disambiguationData":[OSD([sQuery(id+"F0.wireOp",EDGE,"E1.5.4.2")])]})]});
            var Q54;
            Q54=makeQuery(id+"F3.boolean.opBoolean","INTERSECT",EDGE,{"derivedFrom":[makeQuery(id+"F2.opExtrude","CAP_FACE",FACE,{"disambiguationData":[OSD([sQuery(id+"F1.wireOp",EDGE,"E2.bottom"),sQuery(id+"F1.wireOp",EDGE,"E2.top"),sQuery(id+"F1.wireOp",EDGE,"E2.left"),sQuery(id+"F1.wireOp",EDGE,"E2.right")])],"isStart":false}),makeQuery(id+"F3.opExtrude","SWEPT_FACE",FACE,{"disambiguationData":[OSD([sQuery(id+"F0.wireOp",EDGE,"E1.4.4.1")])]})]});
            var Q55;
            Q55=makeQuery(id+"F3.boolean.opBoolean","INTERSECT",EDGE,{"derivedFrom":[makeQuery(id+"F2.opExtrude","CAP_FACE",FACE,{"disambiguationData":[OSD([sQuery(id+"F1.wireOp",EDGE,"E2.bottom"),sQuery(id+"F1.wireOp",EDGE,"E2.top"),sQuery(id+"F1.wireOp",EDGE,"E2.left"),sQuery(id+"F1.wireOp",EDGE,"E2.right")])],"isStart":false}),makeQuery(id+"F3.opExtrude","SWEPT_FACE",FACE,{"disambiguationData":[OSD([sQuery(id+"F0.wireOp",EDGE,"E1.4.4.2")])]})]});
            var Q56;
            Q56=makeQuery(id+"F3.boolean.opBoolean","INTERSECT",EDGE,{"derivedFrom":[makeQuery(id+"F2.opExtrude","CAP_FACE",FACE,{"disambiguationData":[OSD([sQuery(id+"F1.wireOp",EDGE,"E2.bottom"),sQuery(id+"F1.wireOp",EDGE,"E2.top"),sQuery(id+"F1.wireOp",EDGE,"E2.left"),sQuery(id+"F1.wireOp",EDGE,"E2.right")])],"isStart":false}),makeQuery(id+"F3.opExtrude","SWEPT_FACE",FACE,{"disambiguationData":[OSD([sQuery(id+"F0.wireOp",EDGE,"E1.3.4.1")])]})]});
            var Q57;
            Q57=makeQuery(id+"F3.boolean.opBoolean","INTERSECT",EDGE,{"derivedFrom":[makeQuery(id+"F2.opExtrude","CAP_FACE",FACE,{"disambiguationData":[OSD([sQuery(id+"F1.wireOp",EDGE,"E2.bottom"),sQuery(id+"F1.wireOp",EDGE,"E2.top"),sQuery(id+"F1.wireOp",EDGE,"E2.left"),sQuery(id+"F1.wireOp",EDGE,"E2.right")])],"isStart":false}),makeQuery(id+"F3.opExtrude","SWEPT_FACE",FACE,{"disambiguationData":[OSD([sQuery(id+"F0.wireOp",EDGE,"E1.3.4.2")])]})]});
            var Q58;
            Q58=makeQuery(id+"F3.boolean.opBoolean","INTERSECT",EDGE,{"derivedFrom":[makeQuery(id+"F2.opExtrude","CAP_FACE",FACE,{"disambiguationData":[OSD([sQuery(id+"F1.wireOp",EDGE,"E2.bottom"),sQuery(id+"F1.wireOp",EDGE,"E2.top"),sQuery(id+"F1.wireOp",EDGE,"E2.left"),sQuery(id+"F1.wireOp",EDGE,"E2.right")])],"isStart":false}),makeQuery(id+"F3.opExtrude","SWEPT_FACE",FACE,{"disambiguationData":[OSD([sQuery(id+"F0.wireOp",EDGE,"E1.2.4.2")])]})]});
            var Q59;
            Q59=makeQuery(id+"F3.boolean.opBoolean","INTERSECT",EDGE,{"derivedFrom":[makeQuery(id+"F2.opExtrude","CAP_FACE",FACE,{"disambiguationData":[OSD([sQuery(id+"F1.wireOp",EDGE,"E2.bottom"),sQuery(id+"F1.wireOp",EDGE,"E2.top"),sQuery(id+"F1.wireOp",EDGE,"E2.left"),sQuery(id+"F1.wireOp",EDGE,"E2.right")])],"isStart":false}),makeQuery(id+"F3.opExtrude","SWEPT_FACE",FACE,{"disambiguationData":[OSD([sQuery(id+"F0.wireOp",EDGE,"E1.1.4.1")])]})]});
            var Q60;
            Q60=makeQuery(id+"F3.boolean.opBoolean","INTERSECT",EDGE,{"derivedFrom":[makeQuery(id+"F2.opExtrude","CAP_FACE",FACE,{"disambiguationData":[OSD([sQuery(id+"F1.wireOp",EDGE,"E2.bottom"),sQuery(id+"F1.wireOp",EDGE,"E2.top"),sQuery(id+"F1.wireOp",EDGE,"E2.left"),sQuery(id+"F1.wireOp",EDGE,"E2.right")])],"isStart":false}),makeQuery(id+"F3.opExtrude","SWEPT_FACE",FACE,{"disambiguationData":[OSD([sQuery(id+"F0.wireOp",EDGE,"E1.1.4.2")])]})]});
            var Q61;
            Q61=makeQuery(id+"F3.boolean.opBoolean","INTERSECT",EDGE,{"derivedFrom":[makeQuery(id+"F2.opExtrude","CAP_FACE",FACE,{"disambiguationData":[OSD([sQuery(id+"F1.wireOp",EDGE,"E2.bottom"),sQuery(id+"F1.wireOp",EDGE,"E2.top"),sQuery(id+"F1.wireOp",EDGE,"E2.left"),sQuery(id+"F1.wireOp",EDGE,"E2.right")])],"isStart":false}),makeQuery(id+"F3.opExtrude","SWEPT_FACE",FACE,{"disambiguationData":[OSD([sQuery(id+"F0.wireOp",EDGE,"E1.0.4.1")])]})]});
            var Q62;
            Q62=makeQuery(id+"F3.boolean.opBoolean","INTERSECT",EDGE,{"derivedFrom":[makeQuery(id+"F2.opExtrude","CAP_FACE",FACE,{"disambiguationData":[OSD([sQuery(id+"F1.wireOp",EDGE,"E2.bottom"),sQuery(id+"F1.wireOp",EDGE,"E2.top"),sQuery(id+"F1.wireOp",EDGE,"E2.left"),sQuery(id+"F1.wireOp",EDGE,"E2.right")])],"isStart":false}),makeQuery(id+"F3.opExtrude","SWEPT_FACE",FACE,{"disambiguationData":[OSD([sQuery(id+"F0.wireOp",EDGE,"E1.0.4.2")])]})]});
            var Q63;
            Q63=makeQuery(id+"F3.boolean.opBoolean","INTERSECT",EDGE,{"derivedFrom":[makeQuery(id+"F2.opExtrude","CAP_FACE",FACE,{"disambiguationData":[OSD([sQuery(id+"F1.wireOp",EDGE,"E2.bottom"),sQuery(id+"F1.wireOp",EDGE,"E2.top"),sQuery(id+"F1.wireOp",EDGE,"E2.left"),sQuery(id+"F1.wireOp",EDGE,"E2.right")])],"isStart":false}),makeQuery(id+"F3.opExtrude","SWEPT_FACE",FACE,{"disambiguationData":[OSD([sQuery(id+"F0.wireOp",EDGE,"E1.0.5.2")])]})]});
            var Q64;
            Q64=makeQuery(id+"F3.boolean.opBoolean","INTERSECT",EDGE,{"derivedFrom":[makeQuery(id+"F2.opExtrude","CAP_FACE",FACE,{"disambiguationData":[OSD([sQuery(id+"F1.wireOp",EDGE,"E2.bottom"),sQuery(id+"F1.wireOp",EDGE,"E2.top"),sQuery(id+"F1.wireOp",EDGE,"E2.left"),sQuery(id+"F1.wireOp",EDGE,"E2.right")])],"isStart":false}),makeQuery(id+"F3.opExtrude","SWEPT_FACE",FACE,{"disambiguationData":[OSD([sQuery(id+"F0.wireOp",EDGE,"E1.0.5.1")])]})]});
            var Q65;
            Q65=makeQuery(id+"F3.boolean.opBoolean","INTERSECT",EDGE,{"derivedFrom":[makeQuery(id+"F2.opExtrude","CAP_FACE",FACE,{"disambiguationData":[OSD([sQuery(id+"F1.wireOp",EDGE,"E2.bottom"),sQuery(id+"F1.wireOp",EDGE,"E2.top"),sQuery(id+"F1.wireOp",EDGE,"E2.left"),sQuery(id+"F1.wireOp",EDGE,"E2.right")])],"isStart":false}),makeQuery(id+"F3.opExtrude","SWEPT_FACE",FACE,{"disambiguationData":[OSD([sQuery(id+"F0.wireOp",EDGE,"E1.1.5.2")])]})]});
            var Q66;
            Q66=makeQuery(id+"F3.boolean.opBoolean","INTERSECT",EDGE,{"derivedFrom":[makeQuery(id+"F2.opExtrude","CAP_FACE",FACE,{"disambiguationData":[OSD([sQuery(id+"F1.wireOp",EDGE,"E2.bottom"),sQuery(id+"F1.wireOp",EDGE,"E2.top"),sQuery(id+"F1.wireOp",EDGE,"E2.left"),sQuery(id+"F1.wireOp",EDGE,"E2.right")])],"isStart":false}),makeQuery(id+"F3.opExtrude","SWEPT_FACE",FACE,{"disambiguationData":[OSD([sQuery(id+"F0.wireOp",EDGE,"E1.1.5.1")])]})]});
            var Q67;
            Q67=makeQuery(id+"F3.boolean.opBoolean","INTERSECT",EDGE,{"derivedFrom":[makeQuery(id+"F2.opExtrude","CAP_FACE",FACE,{"disambiguationData":[OSD([sQuery(id+"F1.wireOp",EDGE,"E2.bottom"),sQuery(id+"F1.wireOp",EDGE,"E2.top"),sQuery(id+"F1.wireOp",EDGE,"E2.left"),sQuery(id+"F1.wireOp",EDGE,"E2.right")])],"isStart":false}),makeQuery(id+"F3.opExtrude","SWEPT_FACE",FACE,{"disambiguationData":[OSD([sQuery(id+"F0.wireOp",EDGE,"E1.2.5.2")])]})]});
            var Q68;
            Q68=makeQuery(id+"F3.boolean.opBoolean","INTERSECT",EDGE,{"derivedFrom":[makeQuery(id+"F2.opExtrude","CAP_FACE",FACE,{"disambiguationData":[OSD([sQuery(id+"F1.wireOp",EDGE,"E2.bottom"),sQuery(id+"F1.wireOp",EDGE,"E2.top"),sQuery(id+"F1.wireOp",EDGE,"E2.left"),sQuery(id+"F1.wireOp",EDGE,"E2.right")])],"isStart":false}),makeQuery(id+"F3.opExtrude","SWEPT_FACE",FACE,{"disambiguationData":[OSD([sQuery(id+"F0.wireOp",EDGE,"E1.2.5.1")])]})]});
            var Q69;
            Q69=makeQuery(id+"F3.boolean.opBoolean","INTERSECT",EDGE,{"derivedFrom":[makeQuery(id+"F2.opExtrude","CAP_FACE",FACE,{"disambiguationData":[OSD([sQuery(id+"F1.wireOp",EDGE,"E2.bottom"),sQuery(id+"F1.wireOp",EDGE,"E2.top"),sQuery(id+"F1.wireOp",EDGE,"E2.left"),sQuery(id+"F1.wireOp",EDGE,"E2.right")])],"isStart":false}),makeQuery(id+"F3.opExtrude","SWEPT_FACE",FACE,{"disambiguationData":[OSD([sQuery(id+"F0.wireOp",EDGE,"E1.3.5.2")])]})]});
            var Q70;
            Q70=makeQuery(id+"F3.boolean.opBoolean","INTERSECT",EDGE,{"derivedFrom":[makeQuery(id+"F2.opExtrude","CAP_FACE",FACE,{"disambiguationData":[OSD([sQuery(id+"F1.wireOp",EDGE,"E2.bottom"),sQuery(id+"F1.wireOp",EDGE,"E2.top"),sQuery(id+"F1.wireOp",EDGE,"E2.left"),sQuery(id+"F1.wireOp",EDGE,"E2.right")])],"isStart":false}),makeQuery(id+"F3.opExtrude","SWEPT_FACE",FACE,{"disambiguationData":[OSD([sQuery(id+"F0.wireOp",EDGE,"E1.3.5.1")])]})]});
            var Q71;
            Q71=makeQuery(id+"F3.boolean.opBoolean","INTERSECT",EDGE,{"derivedFrom":[makeQuery(id+"F2.opExtrude","CAP_FACE",FACE,{"disambiguationData":[OSD([sQuery(id+"F1.wireOp",EDGE,"E2.bottom"),sQuery(id+"F1.wireOp",EDGE,"E2.top"),sQuery(id+"F1.wireOp",EDGE,"E2.left"),sQuery(id+"F1.wireOp",EDGE,"E2.right")])],"isStart":false}),makeQuery(id+"F3.opExtrude","SWEPT_FACE",FACE,{"disambiguationData":[OSD([sQuery(id+"F0.wireOp",EDGE,"E1.4.5.2")])]})]});
            var Q72;
            Q72=makeQuery(id+"F3.boolean.opBoolean","INTERSECT",EDGE,{"derivedFrom":[makeQuery(id+"F2.opExtrude","CAP_FACE",FACE,{"disambiguationData":[OSD([sQuery(id+"F1.wireOp",EDGE,"E2.bottom"),sQuery(id+"F1.wireOp",EDGE,"E2.top"),sQuery(id+"F1.wireOp",EDGE,"E2.left"),sQuery(id+"F1.wireOp",EDGE,"E2.right")])],"isStart":false}),makeQuery(id+"F3.opExtrude","SWEPT_FACE",FACE,{"disambiguationData":[OSD([sQuery(id+"F0.wireOp",EDGE,"E1.4.5.1")])]})]});
            var Q73;
            Q73=makeQuery(id+"F3.boolean.opBoolean","INTERSECT",EDGE,{"derivedFrom":[makeQuery(id+"F2.opExtrude","CAP_FACE",FACE,{"disambiguationData":[OSD([sQuery(id+"F1.wireOp",EDGE,"E2.bottom"),sQuery(id+"F1.wireOp",EDGE,"E2.top"),sQuery(id+"F1.wireOp",EDGE,"E2.left"),sQuery(id+"F1.wireOp",EDGE,"E2.right")])],"isStart":false}),makeQuery(id+"F3.opExtrude","SWEPT_FACE",FACE,{"disambiguationData":[OSD([sQuery(id+"F0.wireOp",EDGE,"E1.5.5.2")])]})]});
            var Q74;
            Q74=makeQuery(id+"F3.boolean.opBoolean","INTERSECT",EDGE,{"derivedFrom":[makeQuery(id+"F2.opExtrude","CAP_FACE",FACE,{"disambiguationData":[OSD([sQuery(id+"F1.wireOp",EDGE,"E2.bottom"),sQuery(id+"F1.wireOp",EDGE,"E2.top"),sQuery(id+"F1.wireOp",EDGE,"E2.left"),sQuery(id+"F1.wireOp",EDGE,"E2.right")])],"isStart":false}),makeQuery(id+"F3.opExtrude","SWEPT_FACE",FACE,{"disambiguationData":[OSD([sQuery(id+"F0.wireOp",EDGE,"E1.5.5.1")])]})]});
            var Q75;
            Q75=makeQuery(id+"F3.boolean.opBoolean","INTERSECT",EDGE,{"derivedFrom":[makeQuery(id+"F2.opExtrude","CAP_FACE",FACE,{"disambiguationData":[OSD([sQuery(id+"F1.wireOp",EDGE,"E2.bottom"),sQuery(id+"F1.wireOp",EDGE,"E2.top"),sQuery(id+"F1.wireOp",EDGE,"E2.left"),sQuery(id+"F1.wireOp",EDGE,"E2.right")])],"isStart":false}),makeQuery(id+"F3.opExtrude","SWEPT_FACE",FACE,{"disambiguationData":[OSD([sQuery(id+"F0.wireOp",EDGE,"E1.2.4.1")])]})]});
            var Q76;
            Q76=makeQuery(id+"F3.boolean.opBoolean","INTERSECT",EDGE,{"derivedFrom":[makeQuery(id+"F2.opExtrude","CAP_FACE",FACE,{"disambiguationData":[OSD([sQuery(id+"F1.wireOp",EDGE,"E2.bottom"),sQuery(id+"F1.wireOp",EDGE,"E2.top"),sQuery(id+"F1.wireOp",EDGE,"E2.left"),sQuery(id+"F1.wireOp",EDGE,"E2.right")])],"isStart":false}),makeQuery(id+"F3.opExtrude","SWEPT_FACE",FACE,{"disambiguationData":[OSD([sQuery(id+"F0.wireOp",EDGE,"E1.5.5.3")])]})]});
            var Q77;
            Q77=makeQuery(id+"F3.boolean.opBoolean","INTERSECT",EDGE,{"derivedFrom":[makeQuery(id+"F2.opExtrude","CAP_FACE",FACE,{"disambiguationData":[OSD([sQuery(id+"F1.wireOp",EDGE,"E2.bottom"),sQuery(id+"F1.wireOp",EDGE,"E2.top"),sQuery(id+"F1.wireOp",EDGE,"E2.left"),sQuery(id+"F1.wireOp",EDGE,"E2.right")])],"isStart":false}),makeQuery(id+"F3.opExtrude","SWEPT_FACE",FACE,{"disambiguationData":[OSD([sQuery(id+"F0.wireOp",EDGE,"E1.4.5.3")])]})]});
            var Q78;
            Q78=makeQuery(id+"F3.boolean.opBoolean","INTERSECT",EDGE,{"derivedFrom":[makeQuery(id+"F2.opExtrude","CAP_FACE",FACE,{"disambiguationData":[OSD([sQuery(id+"F1.wireOp",EDGE,"E2.bottom"),sQuery(id+"F1.wireOp",EDGE,"E2.top"),sQuery(id+"F1.wireOp",EDGE,"E2.left"),sQuery(id+"F1.wireOp",EDGE,"E2.right")])],"isStart":false}),makeQuery(id+"F3.opExtrude","SWEPT_FACE",FACE,{"disambiguationData":[OSD([sQuery(id+"F0.wireOp",EDGE,"E1.3.5.3")])]})]});
            var Q79;
            Q79=makeQuery(id+"F3.boolean.opBoolean","INTERSECT",EDGE,{"derivedFrom":[makeQuery(id+"F2.opExtrude","CAP_FACE",FACE,{"disambiguationData":[OSD([sQuery(id+"F1.wireOp",EDGE,"E2.bottom"),sQuery(id+"F1.wireOp",EDGE,"E2.top"),sQuery(id+"F1.wireOp",EDGE,"E2.left"),sQuery(id+"F1.wireOp",EDGE,"E2.right")])],"isStart":false}),makeQuery(id+"F3.opExtrude","SWEPT_FACE",FACE,{"disambiguationData":[OSD([sQuery(id+"F0.wireOp",EDGE,"E1.2.5.3")])]})]});
            var Q80;
            Q80=makeQuery(id+"F3.boolean.opBoolean","INTERSECT",EDGE,{"derivedFrom":[makeQuery(id+"F2.opExtrude","CAP_FACE",FACE,{"disambiguationData":[OSD([sQuery(id+"F1.wireOp",EDGE,"E2.bottom"),sQuery(id+"F1.wireOp",EDGE,"E2.top"),sQuery(id+"F1.wireOp",EDGE,"E2.left"),sQuery(id+"F1.wireOp",EDGE,"E2.right")])],"isStart":false}),makeQuery(id+"F3.opExtrude","SWEPT_FACE",FACE,{"disambiguationData":[OSD([sQuery(id+"F0.wireOp",EDGE,"E1.1.5.3")])]})]});
            var Q81;
            Q81=makeQuery(id+"F3.boolean.opBoolean","INTERSECT",EDGE,{"derivedFrom":[makeQuery(id+"F2.opExtrude","CAP_FACE",FACE,{"disambiguationData":[OSD([sQuery(id+"F1.wireOp",EDGE,"E2.bottom"),sQuery(id+"F1.wireOp",EDGE,"E2.top"),sQuery(id+"F1.wireOp",EDGE,"E2.left"),sQuery(id+"F1.wireOp",EDGE,"E2.right")])],"isStart":false}),makeQuery(id+"F3.opExtrude","SWEPT_FACE",FACE,{"disambiguationData":[OSD([sQuery(id+"F0.wireOp",EDGE,"E1.0.5.3")])]})]});
            var Q82;
            Q82=makeQuery(id+"F3.boolean.opBoolean","INTERSECT",EDGE,{"derivedFrom":[makeQuery(id+"F2.opExtrude","CAP_FACE",FACE,{"disambiguationData":[OSD([sQuery(id+"F1.wireOp",EDGE,"E2.bottom"),sQuery(id+"F1.wireOp",EDGE,"E2.top"),sQuery(id+"F1.wireOp",EDGE,"E2.left"),sQuery(id+"F1.wireOp",EDGE,"E2.right")])],"isStart":false}),makeQuery(id+"F3.opExtrude","SWEPT_FACE",FACE,{"disambiguationData":[OSD([sQuery(id+"F0.wireOp",EDGE,"E1.0.5.0")])]})]});
            var Q83;
            Q83=makeQuery(id+"F3.boolean.opBoolean","INTERSECT",EDGE,{"derivedFrom":[makeQuery(id+"F2.opExtrude","CAP_FACE",FACE,{"disambiguationData":[OSD([sQuery(id+"F1.wireOp",EDGE,"E2.bottom"),sQuery(id+"F1.wireOp",EDGE,"E2.top"),sQuery(id+"F1.wireOp",EDGE,"E2.left"),sQuery(id+"F1.wireOp",EDGE,"E2.right")])],"isStart":false}),makeQuery(id+"F3.opExtrude","SWEPT_FACE",FACE,{"disambiguationData":[OSD([sQuery(id+"F0.wireOp",EDGE,"E1.1.5.0")])]})]});
            var Q84;
            Q84=makeQuery(id+"F3.boolean.opBoolean","INTERSECT",EDGE,{"derivedFrom":[makeQuery(id+"F2.opExtrude","CAP_FACE",FACE,{"disambiguationData":[OSD([sQuery(id+"F1.wireOp",EDGE,"E2.bottom"),sQuery(id+"F1.wireOp",EDGE,"E2.top"),sQuery(id+"F1.wireOp",EDGE,"E2.left"),sQuery(id+"F1.wireOp",EDGE,"E2.right")])],"isStart":false}),makeQuery(id+"F3.opExtrude","SWEPT_FACE",FACE,{"disambiguationData":[OSD([sQuery(id+"F0.wireOp",EDGE,"E1.2.5.0")])]})]});
            var Q85;
            Q85=makeQuery(id+"F3.boolean.opBoolean","INTERSECT",EDGE,{"derivedFrom":[makeQuery(id+"F2.opExtrude","CAP_FACE",FACE,{"disambiguationData":[OSD([sQuery(id+"F1.wireOp",EDGE,"E2.bottom"),sQuery(id+"F1.wireOp",EDGE,"E2.top"),sQuery(id+"F1.wireOp",EDGE,"E2.left"),sQuery(id+"F1.wireOp",EDGE,"E2.right")])],"isStart":false}),makeQuery(id+"F3.opExtrude","SWEPT_FACE",FACE,{"disambiguationData":[OSD([sQuery(id+"F0.wireOp",EDGE,"E1.3.5.0")])]})]});
            var Q86;
            Q86=makeQuery(id+"F3.boolean.opBoolean","INTERSECT",EDGE,{"derivedFrom":[makeQuery(id+"F2.opExtrude","CAP_FACE",FACE,{"disambiguationData":[OSD([sQuery(id+"F1.wireOp",EDGE,"E2.bottom"),sQuery(id+"F1.wireOp",EDGE,"E2.top"),sQuery(id+"F1.wireOp",EDGE,"E2.left"),sQuery(id+"F1.wireOp",EDGE,"E2.right")])],"isStart":false}),makeQuery(id+"F3.opExtrude","SWEPT_FACE",FACE,{"disambiguationData":[OSD([sQuery(id+"F0.wireOp",EDGE,"E1.4.5.0")])]})]});
            var Q87;
            Q87=makeQuery(id+"F3.boolean.opBoolean","INTERSECT",EDGE,{"derivedFrom":[makeQuery(id+"F2.opExtrude","CAP_FACE",FACE,{"disambiguationData":[OSD([sQuery(id+"F1.wireOp",EDGE,"E2.bottom"),sQuery(id+"F1.wireOp",EDGE,"E2.top"),sQuery(id+"F1.wireOp",EDGE,"E2.left"),sQuery(id+"F1.wireOp",EDGE,"E2.right")])],"isStart":false}),makeQuery(id+"F3.opExtrude","SWEPT_FACE",FACE,{"disambiguationData":[OSD([sQuery(id+"F0.wireOp",EDGE,"E1.5.5.0")])]})]});
            var Q88;
            Q88=makeQuery(id+"F3.boolean.opBoolean","INTERSECT",EDGE,{"derivedFrom":[makeQuery(id+"F2.opExtrude","CAP_FACE",FACE,{"disambiguationData":[OSD([sQuery(id+"F1.wireOp",EDGE,"E2.bottom"),sQuery(id+"F1.wireOp",EDGE,"E2.top"),sQuery(id+"F1.wireOp",EDGE,"E2.left"),sQuery(id+"F1.wireOp",EDGE,"E2.right")])],"isStart":false}),makeQuery(id+"F3.opExtrude","SWEPT_FACE",FACE,{"disambiguationData":[OSD([sQuery(id+"F0.wireOp",EDGE,"E1.5.4.3")])]})]});
            var Q89;
            Q89=makeQuery(id+"F3.boolean.opBoolean","INTERSECT",EDGE,{"derivedFrom":[makeQuery(id+"F2.opExtrude","CAP_FACE",FACE,{"disambiguationData":[OSD([sQuery(id+"F1.wireOp",EDGE,"E2.bottom"),sQuery(id+"F1.wireOp",EDGE,"E2.top"),sQuery(id+"F1.wireOp",EDGE,"E2.left"),sQuery(id+"F1.wireOp",EDGE,"E2.right")])],"isStart":false}),makeQuery(id+"F3.opExtrude","SWEPT_FACE",FACE,{"disambiguationData":[OSD([sQuery(id+"F0.wireOp",EDGE,"E1.4.4.3")])]})]});
            var Q90;
            Q90=makeQuery(id+"F3.boolean.opBoolean","INTERSECT",EDGE,{"derivedFrom":[makeQuery(id+"F2.opExtrude","CAP_FACE",FACE,{"disambiguationData":[OSD([sQuery(id+"F1.wireOp",EDGE,"E2.bottom"),sQuery(id+"F1.wireOp",EDGE,"E2.top"),sQuery(id+"F1.wireOp",EDGE,"E2.left"),sQuery(id+"F1.wireOp",EDGE,"E2.right")])],"isStart":false}),makeQuery(id+"F3.opExtrude","SWEPT_FACE",FACE,{"disambiguationData":[OSD([sQuery(id+"F0.wireOp",EDGE,"E1.3.4.3")])]})]});
            var Q91;
            Q91=makeQuery(id+"F3.boolean.opBoolean","INTERSECT",EDGE,{"derivedFrom":[makeQuery(id+"F2.opExtrude","CAP_FACE",FACE,{"disambiguationData":[OSD([sQuery(id+"F1.wireOp",EDGE,"E2.bottom"),sQuery(id+"F1.wireOp",EDGE,"E2.top"),sQuery(id+"F1.wireOp",EDGE,"E2.left"),sQuery(id+"F1.wireOp",EDGE,"E2.right")])],"isStart":false}),makeQuery(id+"F3.opExtrude","SWEPT_FACE",FACE,{"disambiguationData":[OSD([sQuery(id+"F0.wireOp",EDGE,"E1.2.4.3")])]})]});
            var Q92;
            Q92=makeQuery(id+"F3.boolean.opBoolean","INTERSECT",EDGE,{"derivedFrom":[makeQuery(id+"F2.opExtrude","CAP_FACE",FACE,{"disambiguationData":[OSD([sQuery(id+"F1.wireOp",EDGE,"E2.bottom"),sQuery(id+"F1.wireOp",EDGE,"E2.top"),sQuery(id+"F1.wireOp",EDGE,"E2.left"),sQuery(id+"F1.wireOp",EDGE,"E2.right")])],"isStart":false}),makeQuery(id+"F3.opExtrude","SWEPT_FACE",FACE,{"disambiguationData":[OSD([sQuery(id+"F0.wireOp",EDGE,"E1.1.4.3")])]})]});
            var Q93;
            Q93=makeQuery(id+"F3.boolean.opBoolean","INTERSECT",EDGE,{"derivedFrom":[makeQuery(id+"F2.opExtrude","CAP_FACE",FACE,{"disambiguationData":[OSD([sQuery(id+"F1.wireOp",EDGE,"E2.bottom"),sQuery(id+"F1.wireOp",EDGE,"E2.top"),sQuery(id+"F1.wireOp",EDGE,"E2.left"),sQuery(id+"F1.wireOp",EDGE,"E2.right")])],"isStart":false}),makeQuery(id+"F3.opExtrude","SWEPT_FACE",FACE,{"disambiguationData":[OSD([sQuery(id+"F0.wireOp",EDGE,"E1.0.4.3")])]})]});
            var Q94;
            Q94=makeQuery(id+"F3.boolean.opBoolean","INTERSECT",EDGE,{"derivedFrom":[makeQuery(id+"F2.opExtrude","CAP_FACE",FACE,{"disambiguationData":[OSD([sQuery(id+"F1.wireOp",EDGE,"E2.bottom"),sQuery(id+"F1.wireOp",EDGE,"E2.top"),sQuery(id+"F1.wireOp",EDGE,"E2.left"),sQuery(id+"F1.wireOp",EDGE,"E2.right")])],"isStart":false}),makeQuery(id+"F3.opExtrude","SWEPT_FACE",FACE,{"disambiguationData":[OSD([sQuery(id+"F0.wireOp",EDGE,"E1.0.3.3")])]})]});
            var Q95;
            Q95=makeQuery(id+"F3.boolean.opBoolean","INTERSECT",EDGE,{"derivedFrom":[makeQuery(id+"F2.opExtrude","CAP_FACE",FACE,{"disambiguationData":[OSD([sQuery(id+"F1.wireOp",EDGE,"E2.bottom"),sQuery(id+"F1.wireOp",EDGE,"E2.top"),sQuery(id+"F1.wireOp",EDGE,"E2.left"),sQuery(id+"F1.wireOp",EDGE,"E2.right")])],"isStart":false}),makeQuery(id+"F3.opExtrude","SWEPT_FACE",FACE,{"disambiguationData":[OSD([sQuery(id+"F0.wireOp",EDGE,"E1.1.3.3")])]})]});
            var Q96;
            Q96=makeQuery(id+"F3.boolean.opBoolean","INTERSECT",EDGE,{"derivedFrom":[makeQuery(id+"F2.opExtrude","CAP_FACE",FACE,{"disambiguationData":[OSD([sQuery(id+"F1.wireOp",EDGE,"E2.bottom"),sQuery(id+"F1.wireOp",EDGE,"E2.top"),sQuery(id+"F1.wireOp",EDGE,"E2.left"),sQuery(id+"F1.wireOp",EDGE,"E2.right")])],"isStart":false}),makeQuery(id+"F3.opExtrude","SWEPT_FACE",FACE,{"disambiguationData":[OSD([sQuery(id+"F0.wireOp",EDGE,"E1.2.3.3")])]})]});
            var Q97;
            Q97=makeQuery(id+"F3.boolean.opBoolean","INTERSECT",EDGE,{"derivedFrom":[makeQuery(id+"F2.opExtrude","CAP_FACE",FACE,{"disambiguationData":[OSD([sQuery(id+"F1.wireOp",EDGE,"E2.bottom"),sQuery(id+"F1.wireOp",EDGE,"E2.top"),sQuery(id+"F1.wireOp",EDGE,"E2.left"),sQuery(id+"F1.wireOp",EDGE,"E2.right")])],"isStart":false}),makeQuery(id+"F3.opExtrude","SWEPT_FACE",FACE,{"disambiguationData":[OSD([sQuery(id+"F0.wireOp",EDGE,"E1.3.3.3")])]})]});
            var Q98;
            Q98=makeQuery(id+"F3.boolean.opBoolean","INTERSECT",EDGE,{"derivedFrom":[makeQuery(id+"F2.opExtrude","CAP_FACE",FACE,{"disambiguationData":[OSD([sQuery(id+"F1.wireOp",EDGE,"E2.bottom"),sQuery(id+"F1.wireOp",EDGE,"E2.top"),sQuery(id+"F1.wireOp",EDGE,"E2.left"),sQuery(id+"F1.wireOp",EDGE,"E2.right")])],"isStart":false}),makeQuery(id+"F3.opExtrude","SWEPT_FACE",FACE,{"disambiguationData":[OSD([sQuery(id+"F0.wireOp",EDGE,"E1.4.3.3")])]})]});
            var Q99;
            Q99=makeQuery(id+"F3.boolean.opBoolean","INTERSECT",EDGE,{"derivedFrom":[makeQuery(id+"F2.opExtrude","CAP_FACE",FACE,{"disambiguationData":[OSD([sQuery(id+"F1.wireOp",EDGE,"E2.bottom"),sQuery(id+"F1.wireOp",EDGE,"E2.top"),sQuery(id+"F1.wireOp",EDGE,"E2.left"),sQuery(id+"F1.wireOp",EDGE,"E2.right")])],"isStart":false}),makeQuery(id+"F3.opExtrude","SWEPT_FACE",FACE,{"disambiguationData":[OSD([sQuery(id+"F0.wireOp",EDGE,"E1.5.3.3")])]})]});
            var Q100;
            Q100=makeQuery(id+"F3.boolean.opBoolean","INTERSECT",EDGE,{"derivedFrom":[makeQuery(id+"F2.opExtrude","CAP_FACE",FACE,{"disambiguationData":[OSD([sQuery(id+"F1.wireOp",EDGE,"E2.bottom"),sQuery(id+"F1.wireOp",EDGE,"E2.top"),sQuery(id+"F1.wireOp",EDGE,"E2.left"),sQuery(id+"F1.wireOp",EDGE,"E2.right")])],"isStart":false}),makeQuery(id+"F3.opExtrude","SWEPT_FACE",FACE,{"disambiguationData":[OSD([sQuery(id+"F0.wireOp",EDGE,"E1.5.2.3")])]})]});
            var Q101;
            Q101=makeQuery(id+"F3.boolean.opBoolean","INTERSECT",EDGE,{"derivedFrom":[makeQuery(id+"F2.opExtrude","CAP_FACE",FACE,{"disambiguationData":[OSD([sQuery(id+"F1.wireOp",EDGE,"E2.bottom"),sQuery(id+"F1.wireOp",EDGE,"E2.top"),sQuery(id+"F1.wireOp",EDGE,"E2.left"),sQuery(id+"F1.wireOp",EDGE,"E2.right")])],"isStart":false}),makeQuery(id+"F3.opExtrude","SWEPT_FACE",FACE,{"disambiguationData":[OSD([sQuery(id+"F0.wireOp",EDGE,"E1.4.2.3")])]})]});
            var Q102;
            Q102=makeQuery(id+"F3.boolean.opBoolean","INTERSECT",EDGE,{"derivedFrom":[makeQuery(id+"F2.opExtrude","CAP_FACE",FACE,{"disambiguationData":[OSD([sQuery(id+"F1.wireOp",EDGE,"E2.bottom"),sQuery(id+"F1.wireOp",EDGE,"E2.top"),sQuery(id+"F1.wireOp",EDGE,"E2.left"),sQuery(id+"F1.wireOp",EDGE,"E2.right")])],"isStart":false}),makeQuery(id+"F3.opExtrude","SWEPT_FACE",FACE,{"disambiguationData":[OSD([sQuery(id+"F0.wireOp",EDGE,"E1.3.2.3")])]})]});
            var Q103;
            Q103=makeQuery(id+"F3.boolean.opBoolean","INTERSECT",EDGE,{"derivedFrom":[makeQuery(id+"F2.opExtrude","CAP_FACE",FACE,{"disambiguationData":[OSD([sQuery(id+"F1.wireOp",EDGE,"E2.bottom"),sQuery(id+"F1.wireOp",EDGE,"E2.top"),sQuery(id+"F1.wireOp",EDGE,"E2.left"),sQuery(id+"F1.wireOp",EDGE,"E2.right")])],"isStart":false}),makeQuery(id+"F3.opExtrude","SWEPT_FACE",FACE,{"disambiguationData":[OSD([sQuery(id+"F0.wireOp",EDGE,"E1.2.2.3")])]})]});
            var Q104;
            Q104=makeQuery(id+"F3.boolean.opBoolean","INTERSECT",EDGE,{"derivedFrom":[makeQuery(id+"F2.opExtrude","CAP_FACE",FACE,{"disambiguationData":[OSD([sQuery(id+"F1.wireOp",EDGE,"E2.bottom"),sQuery(id+"F1.wireOp",EDGE,"E2.top"),sQuery(id+"F1.wireOp",EDGE,"E2.left"),sQuery(id+"F1.wireOp",EDGE,"E2.right")])],"isStart":false}),makeQuery(id+"F3.opExtrude","SWEPT_FACE",FACE,{"disambiguationData":[OSD([sQuery(id+"F0.wireOp",EDGE,"E1.1.2.3")])]})]});
            var Q105;
            Q105=makeQuery(id+"F3.boolean.opBoolean","INTERSECT",EDGE,{"derivedFrom":[makeQuery(id+"F2.opExtrude","CAP_FACE",FACE,{"disambiguationData":[OSD([sQuery(id+"F1.wireOp",EDGE,"E2.bottom"),sQuery(id+"F1.wireOp",EDGE,"E2.top"),sQuery(id+"F1.wireOp",EDGE,"E2.left"),sQuery(id+"F1.wireOp",EDGE,"E2.right")])],"isStart":false}),makeQuery(id+"F3.opExtrude","SWEPT_FACE",FACE,{"disambiguationData":[OSD([sQuery(id+"F0.wireOp",EDGE,"E1.0.2.3")])]})]});
            var Q106;
            Q106=makeQuery(id+"F3.boolean.opBoolean","INTERSECT",EDGE,{"derivedFrom":[makeQuery(id+"F2.opExtrude","CAP_FACE",FACE,{"disambiguationData":[OSD([sQuery(id+"F1.wireOp",EDGE,"E2.bottom"),sQuery(id+"F1.wireOp",EDGE,"E2.top"),sQuery(id+"F1.wireOp",EDGE,"E2.left"),sQuery(id+"F1.wireOp",EDGE,"E2.right")])],"isStart":false}),makeQuery(id+"F3.opExtrude","SWEPT_FACE",FACE,{"disambiguationData":[OSD([sQuery(id+"F0.wireOp",EDGE,"E1.0.1.3")])]})]});
            var Q107;
            Q107=makeQuery(id+"F3.boolean.opBoolean","INTERSECT",EDGE,{"derivedFrom":[makeQuery(id+"F2.opExtrude","CAP_FACE",FACE,{"disambiguationData":[OSD([sQuery(id+"F1.wireOp",EDGE,"E2.bottom"),sQuery(id+"F1.wireOp",EDGE,"E2.top"),sQuery(id+"F1.wireOp",EDGE,"E2.left"),sQuery(id+"F1.wireOp",EDGE,"E2.right")])],"isStart":false}),makeQuery(id+"F3.opExtrude","SWEPT_FACE",FACE,{"disambiguationData":[OSD([sQuery(id+"F0.wireOp",EDGE,"E1.1.1.3")])]})]});
            var Q108;
            Q108=makeQuery(id+"F3.boolean.opBoolean","INTERSECT",EDGE,{"derivedFrom":[makeQuery(id+"F2.opExtrude","CAP_FACE",FACE,{"disambiguationData":[OSD([sQuery(id+"F1.wireOp",EDGE,"E2.bottom"),sQuery(id+"F1.wireOp",EDGE,"E2.top"),sQuery(id+"F1.wireOp",EDGE,"E2.left"),sQuery(id+"F1.wireOp",EDGE,"E2.right")])],"isStart":false}),makeQuery(id+"F3.opExtrude","SWEPT_FACE",FACE,{"disambiguationData":[OSD([sQuery(id+"F0.wireOp",EDGE,"E1.2.1.3")])]})]});
            var Q109;
            Q109=makeQuery(id+"F3.boolean.opBoolean","INTERSECT",EDGE,{"derivedFrom":[makeQuery(id+"F2.opExtrude","CAP_FACE",FACE,{"disambiguationData":[OSD([sQuery(id+"F1.wireOp",EDGE,"E2.bottom"),sQuery(id+"F1.wireOp",EDGE,"E2.top"),sQuery(id+"F1.wireOp",EDGE,"E2.left"),sQuery(id+"F1.wireOp",EDGE,"E2.right")])],"isStart":false}),makeQuery(id+"F3.opExtrude","SWEPT_FACE",FACE,{"disambiguationData":[OSD([sQuery(id+"F0.wireOp",EDGE,"E1.3.1.3")])]})]});
            var Q110;
            Q110=makeQuery(id+"F3.boolean.opBoolean","INTERSECT",EDGE,{"derivedFrom":[makeQuery(id+"F2.opExtrude","CAP_FACE",FACE,{"disambiguationData":[OSD([sQuery(id+"F1.wireOp",EDGE,"E2.bottom"),sQuery(id+"F1.wireOp",EDGE,"E2.top"),sQuery(id+"F1.wireOp",EDGE,"E2.left"),sQuery(id+"F1.wireOp",EDGE,"E2.right")])],"isStart":false}),makeQuery(id+"F3.opExtrude","SWEPT_FACE",FACE,{"disambiguationData":[OSD([sQuery(id+"F0.wireOp",EDGE,"E1.4.1.3")])]})]});
            var Q111;
            Q111=makeQuery(id+"F3.boolean.opBoolean","INTERSECT",EDGE,{"derivedFrom":[makeQuery(id+"F2.opExtrude","CAP_FACE",FACE,{"disambiguationData":[OSD([sQuery(id+"F1.wireOp",EDGE,"E2.bottom"),sQuery(id+"F1.wireOp",EDGE,"E2.top"),sQuery(id+"F1.wireOp",EDGE,"E2.left"),sQuery(id+"F1.wireOp",EDGE,"E2.right")])],"isStart":false}),makeQuery(id+"F3.opExtrude","SWEPT_FACE",FACE,{"disambiguationData":[OSD([sQuery(id+"F0.wireOp",EDGE,"E1.5.1.3")])]})]});
            var Q112;
            Q112=makeQuery(id+"F3.boolean.opBoolean","INTERSECT",EDGE,{"derivedFrom":[makeQuery(id+"F2.opExtrude","CAP_FACE",FACE,{"disambiguationData":[OSD([sQuery(id+"F1.wireOp",EDGE,"E2.bottom"),sQuery(id+"F1.wireOp",EDGE,"E2.top"),sQuery(id+"F1.wireOp",EDGE,"E2.left"),sQuery(id+"F1.wireOp",EDGE,"E2.right")])],"isStart":false}),makeQuery(id+"F3.opExtrude","SWEPT_FACE",FACE,{"disambiguationData":[OSD([sQuery(id+"F0.wireOp",EDGE,"E1.5.0.3")])]})]});
            var Q113;
            Q113=makeQuery(id+"F3.boolean.opBoolean","INTERSECT",EDGE,{"derivedFrom":[makeQuery(id+"F2.opExtrude","CAP_FACE",FACE,{"disambiguationData":[OSD([sQuery(id+"F1.wireOp",EDGE,"E2.bottom"),sQuery(id+"F1.wireOp",EDGE,"E2.top"),sQuery(id+"F1.wireOp",EDGE,"E2.left"),sQuery(id+"F1.wireOp",EDGE,"E2.right")])],"isStart":false}),makeQuery(id+"F3.opExtrude","SWEPT_FACE",FACE,{"disambiguationData":[OSD([sQuery(id+"F0.wireOp",EDGE,"E1.4.0.3")])]})]});
            var Q114;
            Q114=makeQuery(id+"F3.boolean.opBoolean","INTERSECT",EDGE,{"derivedFrom":[makeQuery(id+"F2.opExtrude","CAP_FACE",FACE,{"disambiguationData":[OSD([sQuery(id+"F1.wireOp",EDGE,"E2.bottom"),sQuery(id+"F1.wireOp",EDGE,"E2.top"),sQuery(id+"F1.wireOp",EDGE,"E2.left"),sQuery(id+"F1.wireOp",EDGE,"E2.right")])],"isStart":false}),makeQuery(id+"F3.opExtrude","SWEPT_FACE",FACE,{"disambiguationData":[OSD([sQuery(id+"F0.wireOp",EDGE,"E1.3.0.3")])]})]});
            var Q115;
            Q115=makeQuery(id+"F3.boolean.opBoolean","INTERSECT",EDGE,{"derivedFrom":[makeQuery(id+"F2.opExtrude","CAP_FACE",FACE,{"disambiguationData":[OSD([sQuery(id+"F1.wireOp",EDGE,"E2.bottom"),sQuery(id+"F1.wireOp",EDGE,"E2.top"),sQuery(id+"F1.wireOp",EDGE,"E2.left"),sQuery(id+"F1.wireOp",EDGE,"E2.right")])],"isStart":false}),makeQuery(id+"F3.opExtrude","SWEPT_FACE",FACE,{"disambiguationData":[OSD([sQuery(id+"F0.wireOp",EDGE,"E1.2.0.3")])]})]});
            var Q116;
            Q116=makeQuery(id+"F3.boolean.opBoolean","INTERSECT",EDGE,{"derivedFrom":[makeQuery(id+"F2.opExtrude","CAP_FACE",FACE,{"disambiguationData":[OSD([sQuery(id+"F1.wireOp",EDGE,"E2.bottom"),sQuery(id+"F1.wireOp",EDGE,"E2.top"),sQuery(id+"F1.wireOp",EDGE,"E2.left"),sQuery(id+"F1.wireOp",EDGE,"E2.right")])],"isStart":false}),makeQuery(id+"F3.opExtrude","SWEPT_FACE",FACE,{"disambiguationData":[OSD([sQuery(id+"F0.wireOp",EDGE,"E1.0.4.0")])]})]});
            var Q117;
            Q117=makeQuery(id+"F3.boolean.opBoolean","INTERSECT",EDGE,{"derivedFrom":[makeQuery(id+"F2.opExtrude","CAP_FACE",FACE,{"disambiguationData":[OSD([sQuery(id+"F1.wireOp",EDGE,"E2.bottom"),sQuery(id+"F1.wireOp",EDGE,"E2.top"),sQuery(id+"F1.wireOp",EDGE,"E2.left"),sQuery(id+"F1.wireOp",EDGE,"E2.right")])],"isStart":false}),makeQuery(id+"F3.opExtrude","SWEPT_FACE",FACE,{"disambiguationData":[OSD([sQuery(id+"F0.wireOp",EDGE,"E1.1.4.0")])]})]});
            var Q118;
            Q118=makeQuery(id+"F3.boolean.opBoolean","INTERSECT",EDGE,{"derivedFrom":[makeQuery(id+"F2.opExtrude","CAP_FACE",FACE,{"disambiguationData":[OSD([sQuery(id+"F1.wireOp",EDGE,"E2.bottom"),sQuery(id+"F1.wireOp",EDGE,"E2.top"),sQuery(id+"F1.wireOp",EDGE,"E2.left"),sQuery(id+"F1.wireOp",EDGE,"E2.right")])],"isStart":false}),makeQuery(id+"F3.opExtrude","SWEPT_FACE",FACE,{"disambiguationData":[OSD([sQuery(id+"F0.wireOp",EDGE,"E1.2.4.0")])]})]});
            var Q119;
            Q119=makeQuery(id+"F3.boolean.opBoolean","INTERSECT",EDGE,{"derivedFrom":[makeQuery(id+"F2.opExtrude","CAP_FACE",FACE,{"disambiguationData":[OSD([sQuery(id+"F1.wireOp",EDGE,"E2.bottom"),sQuery(id+"F1.wireOp",EDGE,"E2.top"),sQuery(id+"F1.wireOp",EDGE,"E2.left"),sQuery(id+"F1.wireOp",EDGE,"E2.right")])],"isStart":false}),makeQuery(id+"F3.opExtrude","SWEPT_FACE",FACE,{"disambiguationData":[OSD([sQuery(id+"F0.wireOp",EDGE,"E1.3.4.0")])]})]});
            var Q120;
            Q120=makeQuery(id+"F3.boolean.opBoolean","INTERSECT",EDGE,{"derivedFrom":[makeQuery(id+"F2.opExtrude","CAP_FACE",FACE,{"disambiguationData":[OSD([sQuery(id+"F1.wireOp",EDGE,"E2.bottom"),sQuery(id+"F1.wireOp",EDGE,"E2.top"),sQuery(id+"F1.wireOp",EDGE,"E2.left"),sQuery(id+"F1.wireOp",EDGE,"E2.right")])],"isStart":false}),makeQuery(id+"F3.opExtrude","SWEPT_FACE",FACE,{"disambiguationData":[OSD([sQuery(id+"F0.wireOp",EDGE,"E1.4.4.0")])]})]});
            var Q121;
            Q121=makeQuery(id+"F3.boolean.opBoolean","INTERSECT",EDGE,{"derivedFrom":[makeQuery(id+"F2.opExtrude","CAP_FACE",FACE,{"disambiguationData":[OSD([sQuery(id+"F1.wireOp",EDGE,"E2.bottom"),sQuery(id+"F1.wireOp",EDGE,"E2.top"),sQuery(id+"F1.wireOp",EDGE,"E2.left"),sQuery(id+"F1.wireOp",EDGE,"E2.right")])],"isStart":false}),makeQuery(id+"F3.opExtrude","SWEPT_FACE",FACE,{"disambiguationData":[OSD([sQuery(id+"F0.wireOp",EDGE,"E1.5.4.0")])]})]});
            var Q122;
            Q122=makeQuery(id+"F3.boolean.opBoolean","INTERSECT",EDGE,{"derivedFrom":[makeQuery(id+"F2.opExtrude","CAP_FACE",FACE,{"disambiguationData":[OSD([sQuery(id+"F1.wireOp",EDGE,"E2.bottom"),sQuery(id+"F1.wireOp",EDGE,"E2.top"),sQuery(id+"F1.wireOp",EDGE,"E2.left"),sQuery(id+"F1.wireOp",EDGE,"E2.right")])],"isStart":false}),makeQuery(id+"F3.opExtrude","SWEPT_FACE",FACE,{"disambiguationData":[OSD([sQuery(id+"F0.wireOp",EDGE,"E1.5.3.0")])]})]});
            var Q123;
            Q123=makeQuery(id+"F3.boolean.opBoolean","INTERSECT",EDGE,{"derivedFrom":[makeQuery(id+"F2.opExtrude","CAP_FACE",FACE,{"disambiguationData":[OSD([sQuery(id+"F1.wireOp",EDGE,"E2.bottom"),sQuery(id+"F1.wireOp",EDGE,"E2.top"),sQuery(id+"F1.wireOp",EDGE,"E2.left"),sQuery(id+"F1.wireOp",EDGE,"E2.right")])],"isStart":false}),makeQuery(id+"F3.opExtrude","SWEPT_FACE",FACE,{"disambiguationData":[OSD([sQuery(id+"F0.wireOp",EDGE,"E1.4.3.0")])]})]});
            var Q124;
            Q124=makeQuery(id+"F3.boolean.opBoolean","INTERSECT",EDGE,{"derivedFrom":[makeQuery(id+"F2.opExtrude","CAP_FACE",FACE,{"disambiguationData":[OSD([sQuery(id+"F1.wireOp",EDGE,"E2.bottom"),sQuery(id+"F1.wireOp",EDGE,"E2.top"),sQuery(id+"F1.wireOp",EDGE,"E2.left"),sQuery(id+"F1.wireOp",EDGE,"E2.right")])],"isStart":false}),makeQuery(id+"F3.opExtrude","SWEPT_FACE",FACE,{"disambiguationData":[OSD([sQuery(id+"F0.wireOp",EDGE,"E1.3.3.0")])]})]});
            var Q125;
            Q125=makeQuery(id+"F3.boolean.opBoolean","INTERSECT",EDGE,{"derivedFrom":[makeQuery(id+"F2.opExtrude","CAP_FACE",FACE,{"disambiguationData":[OSD([sQuery(id+"F1.wireOp",EDGE,"E2.bottom"),sQuery(id+"F1.wireOp",EDGE,"E2.top"),sQuery(id+"F1.wireOp",EDGE,"E2.left"),sQuery(id+"F1.wireOp",EDGE,"E2.right")])],"isStart":false}),makeQuery(id+"F3.opExtrude","SWEPT_FACE",FACE,{"disambiguationData":[OSD([sQuery(id+"F0.wireOp",EDGE,"E1.2.3.0")])]})]});
            var Q126;
            Q126=makeQuery(id+"F3.boolean.opBoolean","INTERSECT",EDGE,{"derivedFrom":[makeQuery(id+"F2.opExtrude","CAP_FACE",FACE,{"disambiguationData":[OSD([sQuery(id+"F1.wireOp",EDGE,"E2.bottom"),sQuery(id+"F1.wireOp",EDGE,"E2.top"),sQuery(id+"F1.wireOp",EDGE,"E2.left"),sQuery(id+"F1.wireOp",EDGE,"E2.right")])],"isStart":false}),makeQuery(id+"F3.opExtrude","SWEPT_FACE",FACE,{"disambiguationData":[OSD([sQuery(id+"F0.wireOp",EDGE,"E1.1.3.0")])]})]});
            var Q127;
            Q127=makeQuery(id+"F3.boolean.opBoolean","INTERSECT",EDGE,{"derivedFrom":[makeQuery(id+"F2.opExtrude","CAP_FACE",FACE,{"disambiguationData":[OSD([sQuery(id+"F1.wireOp",EDGE,"E2.bottom"),sQuery(id+"F1.wireOp",EDGE,"E2.top"),sQuery(id+"F1.wireOp",EDGE,"E2.left"),sQuery(id+"F1.wireOp",EDGE,"E2.right")])],"isStart":false}),makeQuery(id+"F3.opExtrude","SWEPT_FACE",FACE,{"disambiguationData":[OSD([sQuery(id+"F0.wireOp",EDGE,"E1.0.3.0")])]})]});
            var Q128;
            Q128=makeQuery(id+"F3.boolean.opBoolean","INTERSECT",EDGE,{"derivedFrom":[makeQuery(id+"F2.opExtrude","CAP_FACE",FACE,{"disambiguationData":[OSD([sQuery(id+"F1.wireOp",EDGE,"E2.bottom"),sQuery(id+"F1.wireOp",EDGE,"E2.top"),sQuery(id+"F1.wireOp",EDGE,"E2.left"),sQuery(id+"F1.wireOp",EDGE,"E2.right")])],"isStart":false}),makeQuery(id+"F3.opExtrude","SWEPT_FACE",FACE,{"disambiguationData":[OSD([sQuery(id+"F0.wireOp",EDGE,"E1.0.2.0")])]})]});
            var Q129;
            Q129=makeQuery(id+"F3.boolean.opBoolean","INTERSECT",EDGE,{"derivedFrom":[makeQuery(id+"F2.opExtrude","CAP_FACE",FACE,{"disambiguationData":[OSD([sQuery(id+"F1.wireOp",EDGE,"E2.bottom"),sQuery(id+"F1.wireOp",EDGE,"E2.top"),sQuery(id+"F1.wireOp",EDGE,"E2.left"),sQuery(id+"F1.wireOp",EDGE,"E2.right")])],"isStart":false}),makeQuery(id+"F3.opExtrude","SWEPT_FACE",FACE,{"disambiguationData":[OSD([sQuery(id+"F0.wireOp",EDGE,"E1.1.2.0")])]})]});
            var Q130;
            Q130=makeQuery(id+"F3.boolean.opBoolean","INTERSECT",EDGE,{"derivedFrom":[makeQuery(id+"F2.opExtrude","CAP_FACE",FACE,{"disambiguationData":[OSD([sQuery(id+"F1.wireOp",EDGE,"E2.bottom"),sQuery(id+"F1.wireOp",EDGE,"E2.top"),sQuery(id+"F1.wireOp",EDGE,"E2.left"),sQuery(id+"F1.wireOp",EDGE,"E2.right")])],"isStart":false}),makeQuery(id+"F3.opExtrude","SWEPT_FACE",FACE,{"disambiguationData":[OSD([sQuery(id+"F0.wireOp",EDGE,"E1.2.2.0")])]})]});
            var Q131;
            Q131=makeQuery(id+"F3.boolean.opBoolean","INTERSECT",EDGE,{"derivedFrom":[makeQuery(id+"F2.opExtrude","CAP_FACE",FACE,{"disambiguationData":[OSD([sQuery(id+"F1.wireOp",EDGE,"E2.bottom"),sQuery(id+"F1.wireOp",EDGE,"E2.top"),sQuery(id+"F1.wireOp",EDGE,"E2.left"),sQuery(id+"F1.wireOp",EDGE,"E2.right")])],"isStart":false}),makeQuery(id+"F3.opExtrude","SWEPT_FACE",FACE,{"disambiguationData":[OSD([sQuery(id+"F0.wireOp",EDGE,"E1.3.2.0")])]})]});
            var Q132;
            Q132=makeQuery(id+"F3.boolean.opBoolean","INTERSECT",EDGE,{"derivedFrom":[makeQuery(id+"F2.opExtrude","CAP_FACE",FACE,{"disambiguationData":[OSD([sQuery(id+"F1.wireOp",EDGE,"E2.bottom"),sQuery(id+"F1.wireOp",EDGE,"E2.top"),sQuery(id+"F1.wireOp",EDGE,"E2.left"),sQuery(id+"F1.wireOp",EDGE,"E2.right")])],"isStart":false}),makeQuery(id+"F3.opExtrude","SWEPT_FACE",FACE,{"disambiguationData":[OSD([sQuery(id+"F0.wireOp",EDGE,"E1.4.2.0")])]})]});
            var Q133;
            Q133=makeQuery(id+"F3.boolean.opBoolean","INTERSECT",EDGE,{"derivedFrom":[makeQuery(id+"F2.opExtrude","CAP_FACE",FACE,{"disambiguationData":[OSD([sQuery(id+"F1.wireOp",EDGE,"E2.bottom"),sQuery(id+"F1.wireOp",EDGE,"E2.top"),sQuery(id+"F1.wireOp",EDGE,"E2.left"),sQuery(id+"F1.wireOp",EDGE,"E2.right")])],"isStart":false}),makeQuery(id+"F3.opExtrude","SWEPT_FACE",FACE,{"disambiguationData":[OSD([sQuery(id+"F0.wireOp",EDGE,"E1.5.2.0")])]})]});
            var Q134;
            Q134=makeQuery(id+"F3.boolean.opBoolean","INTERSECT",EDGE,{"derivedFrom":[makeQuery(id+"F2.opExtrude","CAP_FACE",FACE,{"disambiguationData":[OSD([sQuery(id+"F1.wireOp",EDGE,"E2.bottom"),sQuery(id+"F1.wireOp",EDGE,"E2.top"),sQuery(id+"F1.wireOp",EDGE,"E2.left"),sQuery(id+"F1.wireOp",EDGE,"E2.right")])],"isStart":false}),makeQuery(id+"F3.opExtrude","SWEPT_FACE",FACE,{"disambiguationData":[OSD([sQuery(id+"F0.wireOp",EDGE,"E1.5.1.0")])]})]});
            var Q135;
            Q135=makeQuery(id+"F3.boolean.opBoolean","INTERSECT",EDGE,{"derivedFrom":[makeQuery(id+"F2.opExtrude","CAP_FACE",FACE,{"disambiguationData":[OSD([sQuery(id+"F1.wireOp",EDGE,"E2.bottom"),sQuery(id+"F1.wireOp",EDGE,"E2.top"),sQuery(id+"F1.wireOp",EDGE,"E2.left"),sQuery(id+"F1.wireOp",EDGE,"E2.right")])],"isStart":false}),makeQuery(id+"F3.opExtrude","SWEPT_FACE",FACE,{"disambiguationData":[OSD([sQuery(id+"F0.wireOp",EDGE,"E1.4.1.0")])]})]});
            var Q136;
            Q136=makeQuery(id+"F3.boolean.opBoolean","INTERSECT",EDGE,{"derivedFrom":[makeQuery(id+"F2.opExtrude","CAP_FACE",FACE,{"disambiguationData":[OSD([sQuery(id+"F1.wireOp",EDGE,"E2.bottom"),sQuery(id+"F1.wireOp",EDGE,"E2.top"),sQuery(id+"F1.wireOp",EDGE,"E2.left"),sQuery(id+"F1.wireOp",EDGE,"E2.right")])],"isStart":false}),makeQuery(id+"F3.opExtrude","SWEPT_FACE",FACE,{"disambiguationData":[OSD([sQuery(id+"F0.wireOp",EDGE,"E1.3.1.0")])]})]});
            var Q137;
            Q137=makeQuery(id+"F3.boolean.opBoolean","INTERSECT",EDGE,{"derivedFrom":[makeQuery(id+"F2.opExtrude","CAP_FACE",FACE,{"disambiguationData":[OSD([sQuery(id+"F1.wireOp",EDGE,"E2.bottom"),sQuery(id+"F1.wireOp",EDGE,"E2.top"),sQuery(id+"F1.wireOp",EDGE,"E2.left"),sQuery(id+"F1.wireOp",EDGE,"E2.right")])],"isStart":false}),makeQuery(id+"F3.opExtrude","SWEPT_FACE",FACE,{"disambiguationData":[OSD([sQuery(id+"F0.wireOp",EDGE,"E1.2.1.0")])]})]});
            var Q138;
            Q138=makeQuery(id+"F3.boolean.opBoolean","INTERSECT",EDGE,{"derivedFrom":[makeQuery(id+"F2.opExtrude","CAP_FACE",FACE,{"disambiguationData":[OSD([sQuery(id+"F1.wireOp",EDGE,"E2.bottom"),sQuery(id+"F1.wireOp",EDGE,"E2.top"),sQuery(id+"F1.wireOp",EDGE,"E2.left"),sQuery(id+"F1.wireOp",EDGE,"E2.right")])],"isStart":false}),makeQuery(id+"F3.opExtrude","SWEPT_FACE",FACE,{"disambiguationData":[OSD([sQuery(id+"F0.wireOp",EDGE,"E1.1.1.0")])]})]});
            var Q139;
            Q139=makeQuery(id+"F3.boolean.opBoolean","INTERSECT",EDGE,{"derivedFrom":[makeQuery(id+"F2.opExtrude","CAP_FACE",FACE,{"disambiguationData":[OSD([sQuery(id+"F1.wireOp",EDGE,"E2.bottom"),sQuery(id+"F1.wireOp",EDGE,"E2.top"),sQuery(id+"F1.wireOp",EDGE,"E2.left"),sQuery(id+"F1.wireOp",EDGE,"E2.right")])],"isStart":false}),makeQuery(id+"F3.opExtrude","SWEPT_FACE",FACE,{"disambiguationData":[OSD([sQuery(id+"F0.wireOp",EDGE,"E1.0.1.0")])]})]});
            var Q140;
            Q140=makeQuery(id+"F3.boolean.opBoolean","INTERSECT",EDGE,{"derivedFrom":[makeQuery(id+"F2.opExtrude","CAP_FACE",FACE,{"disambiguationData":[OSD([sQuery(id+"F1.wireOp",EDGE,"E2.bottom"),sQuery(id+"F1.wireOp",EDGE,"E2.top"),sQuery(id+"F1.wireOp",EDGE,"E2.left"),sQuery(id+"F1.wireOp",EDGE,"E2.right")])],"isStart":false}),makeQuery(id+"F3.opExtrude","SWEPT_FACE",FACE,{"disambiguationData":[OSD([sQuery(id+"F0.wireOp",EDGE,"E1.5.0.0")])]})]});
            var Q141;
            Q141=makeQuery(id+"F3.boolean.opBoolean","INTERSECT",EDGE,{"derivedFrom":[makeQuery(id+"F2.opExtrude","CAP_FACE",FACE,{"disambiguationData":[OSD([sQuery(id+"F1.wireOp",EDGE,"E2.bottom"),sQuery(id+"F1.wireOp",EDGE,"E2.top"),sQuery(id+"F1.wireOp",EDGE,"E2.left"),sQuery(id+"F1.wireOp",EDGE,"E2.right")])],"isStart":false}),makeQuery(id+"F3.opExtrude","SWEPT_FACE",FACE,{"disambiguationData":[OSD([sQuery(id+"F0.wireOp",EDGE,"E1.4.0.0")])]})]});
            var Q142;
            Q142=makeQuery(id+"F3.boolean.opBoolean","INTERSECT",EDGE,{"derivedFrom":[makeQuery(id+"F2.opExtrude","CAP_FACE",FACE,{"disambiguationData":[OSD([sQuery(id+"F1.wireOp",EDGE,"E2.bottom"),sQuery(id+"F1.wireOp",EDGE,"E2.top"),sQuery(id+"F1.wireOp",EDGE,"E2.left"),sQuery(id+"F1.wireOp",EDGE,"E2.right")])],"isStart":false}),makeQuery(id+"F3.opExtrude","SWEPT_FACE",FACE,{"disambiguationData":[OSD([sQuery(id+"F0.wireOp",EDGE,"E1.3.0.0")])]})]});
            var Q143;
            Q143=makeQuery(id+"F3.boolean.opBoolean","INTERSECT",EDGE,{"derivedFrom":[makeQuery(id+"F2.opExtrude","CAP_FACE",FACE,{"disambiguationData":[OSD([sQuery(id+"F1.wireOp",EDGE,"E2.bottom"),sQuery(id+"F1.wireOp",EDGE,"E2.top"),sQuery(id+"F1.wireOp",EDGE,"E2.left"),sQuery(id+"F1.wireOp",EDGE,"E2.right")])],"isStart":false}),makeQuery(id+"F3.opExtrude","SWEPT_FACE",FACE,{"disambiguationData":[OSD([sQuery(id+"F0.wireOp",EDGE,"E1.2.0.0")])]})]});
            chamfer(context, id + "F4", {"entities" : qUnion([Q0, Q1, Q2, Q3, Q4, Q5, Q6, Q7, Q8, Q9, Q10, Q11, Q12, Q13, Q14, Q15, Q16, Q17, Q18, Q19, Q20, Q21, Q22, Q23, Q24, Q25, Q26, Q27, Q28, Q29, Q30, Q31, Q32, Q33, Q34, Q35, Q36, Q37, Q38, Q39, Q40, Q41, Q42, Q43, Q44, Q45, Q46, Q47, Q48, Q49, Q50, Q51, Q52, Q53, Q54, Q55, Q56, Q57, Q58, Q59, Q60, Q61, Q62, Q63, Q64, Q65, Q66, Q67, Q68, Q69, Q70, Q71, Q72, Q73, Q74, Q75, Q76, Q77, Q78, Q79, Q80, Q81, Q82, Q83, Q84, Q85, Q86, Q87, Q88, Q89, Q90, Q91, Q92, Q93, Q94, Q95, Q96, Q97, Q98, Q99, Q100, Q101, Q102, Q103, Q104, Q105, Q106, Q107, Q108, Q109, Q110, Q111, Q112, Q113, Q114, Q115, Q116, Q117, Q118, Q119, Q120, Q121, Q122, Q123, Q124, Q125, Q126, Q127, Q128, Q129, Q130, Q131, Q132, Q133, Q134, Q135, Q136, Q137, Q138, Q139, Q140, Q141, Q142, Q143]), "width" : 1.5 * mm, "tangentPropagation" : true});
        }
        {
            var Q0;
            Q0=makeQuery(id+"F2.opExtrude","CAP_EDGE",EDGE,{"disambiguationData":[OSD([sQuery(id+"F1.wireOp",EDGE,"E2.bottom")])],"isStart":false});
            var Q1;
            Q1=makeQuery(id+"F2.opExtrude","CAP_EDGE",EDGE,{"disambiguationData":[OSD([sQuery(id+"F1.wireOp",EDGE,"E2.left")])],"isStart":false});
            var Q2;
            Q2=makeQuery(id+"F2.opExtrude","CAP_EDGE",EDGE,{"disambiguationData":[OSD([sQuery(id+"F1.wireOp",EDGE,"E2.top")])],"isStart":false});
            var Q3;
            Q3=makeQuery(id+"F2.opExtrude","CAP_EDGE",EDGE,{"disambiguationData":[OSD([sQuery(id+"F1.wireOp",EDGE,"E2.right")])],"isStart":false});
            fillet(context, id + "F5", {"entities" : qUnion([Q0, Q1, Q2, Q3]), "radius" : 3 * mm, "tangentPropagation" : true, "allowEdgeOverflow" : false});
        }
    });
